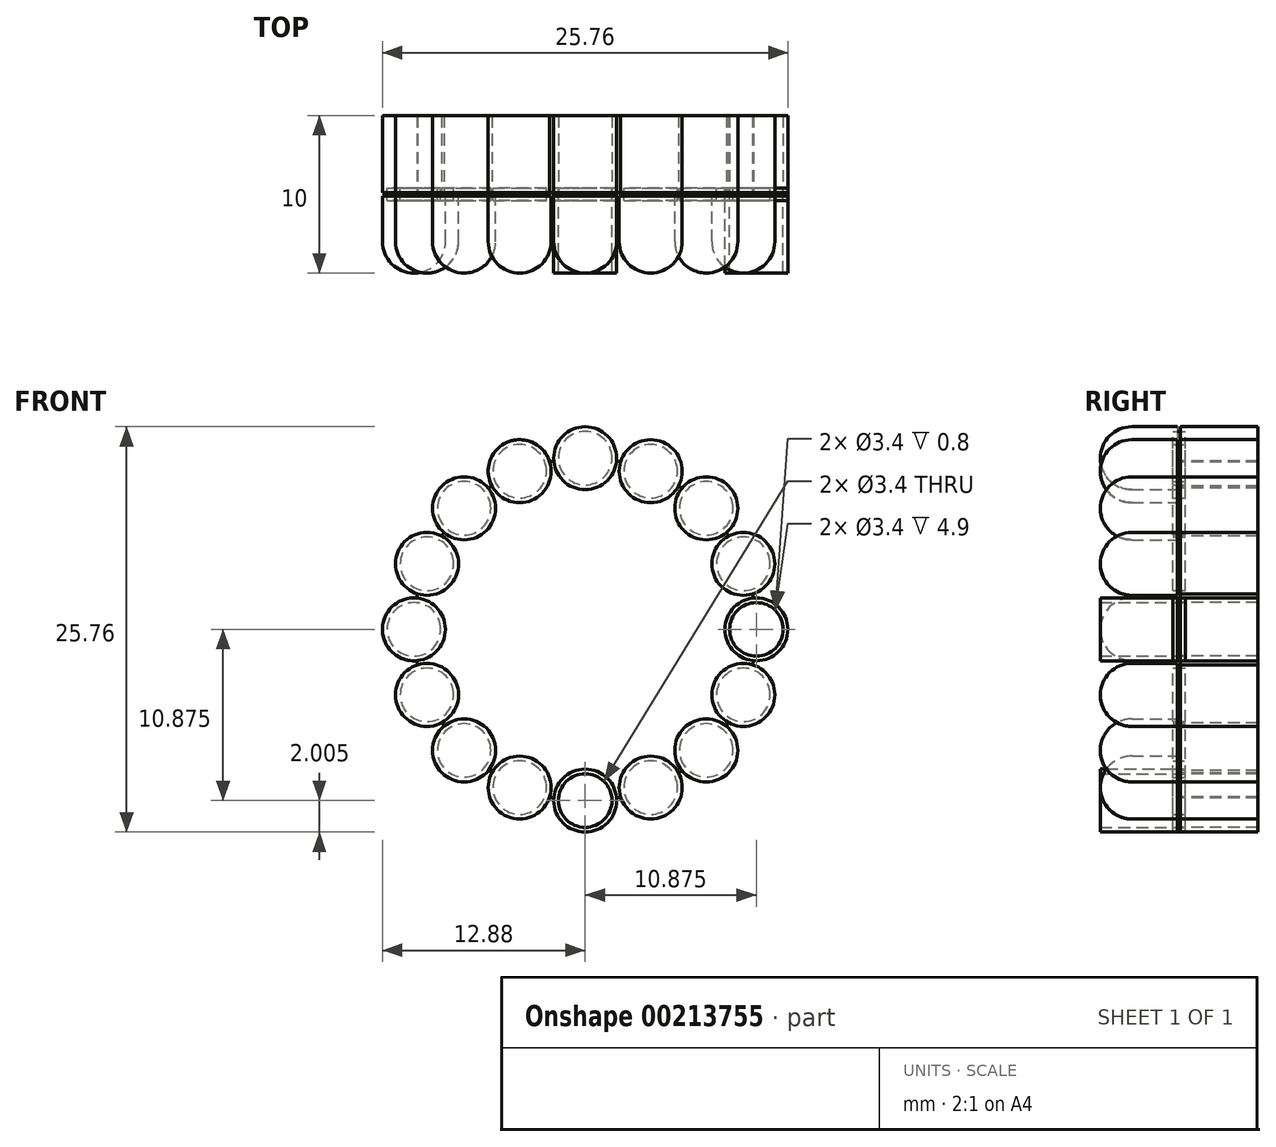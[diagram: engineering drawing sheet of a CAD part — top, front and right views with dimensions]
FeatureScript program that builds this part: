
annotation { "Feature Type Name" : "Feature", "Feature Type Description" : "" }
export const myFeature = defineFeature(function(context is Context, id is Id, definition is map)
    precondition{}
    {
        {
            var Q0;
            Q0=qCreatedBy(makeId("Front.planeOp"),FACE);
            var sketch = newSketch(context, id + "F0", { "sketchPlane" : qUnion([Q0])});
            skCircle(sketch, "E0", {"center": v(0, 0) * mm, "radius": 8.88 * mm, "construction": true});
            skCircle(sketch, "E1.0", {"center": v(0, 0) * mm, "radius": 12.88 * mm, "construction": true});
            skCircle(sketch, "E2.0", {"center": v(0, 0) * mm, "radius": 10.88 * mm});
            skCircle(sketch, "E3", {"center": v(0, 10.88) * mm, "radius": 2 * mm});
            skCircle(sketch, "E4.1.0", {"center": v(-4.16, 10.05) * mm, "radius": 2 * mm});
            skCircle(sketch, "E4.2.0", {"center": v(-7.69, 7.69) * mm, "radius": 2 * mm});
            skCircle(sketch, "E4.3.0", {"center": v(-10.05, 4.16) * mm, "radius": 2 * mm});
            skCircle(sketch, "E4.4.0", {"center": v(-10.88, 0) * mm, "radius": 2 * mm});
            skCircle(sketch, "E4.5.0", {"center": v(-10.05, -4.16) * mm, "radius": 2 * mm});
            skCircle(sketch, "E4.6.0", {"center": v(-7.69, -7.69) * mm, "radius": 2 * mm});
            skCircle(sketch, "E4.7.0", {"center": v(-4.16, -10.05) * mm, "radius": 2 * mm});
            skCircle(sketch, "E4.8.0", {"center": v(0, -10.88) * mm, "radius": 2 * mm});
            skCircle(sketch, "E4.9.0", {"center": v(4.16, -10.05) * mm, "radius": 2 * mm});
            skCircle(sketch, "E4.10.0", {"center": v(7.69, -7.69) * mm, "radius": 2 * mm});
            skCircle(sketch, "E4.11.0", {"center": v(10.05, -4.16) * mm, "radius": 2 * mm});
            skCircle(sketch, "E4.12.0", {"center": v(10.88, 0) * mm, "radius": 2 * mm});
            skCircle(sketch, "E4.13.0", {"center": v(10.05, 4.16) * mm, "radius": 2 * mm});
            skCircle(sketch, "E4.14.0", {"center": v(7.69, 7.69) * mm, "radius": 2 * mm});
            skCircle(sketch, "E4.15.0", {"center": v(4.16, 10.05) * mm, "radius": 2 * mm});
            skCircle(sketch, "E5.0", {"center": v(0, -10.88) * mm, "radius": 1.7 * mm});
            skCircle(sketch, "E6.1.0", {"center": v(4.16, -10.05) * mm, "radius": 1.7 * mm});
            skCircle(sketch, "E6.2.0", {"center": v(7.69, -7.69) * mm, "radius": 1.7 * mm});
            skCircle(sketch, "E6.3.0", {"center": v(10.05, -4.16) * mm, "radius": 1.7 * mm});
            skCircle(sketch, "E6.4.0", {"center": v(10.88, 0) * mm, "radius": 1.7 * mm});
            skCircle(sketch, "E6.5.0", {"center": v(10.05, 4.16) * mm, "radius": 1.7 * mm});
            skCircle(sketch, "E6.6.0", {"center": v(7.69, 7.69) * mm, "radius": 1.7 * mm});
            skCircle(sketch, "E6.7.0", {"center": v(4.16, 10.05) * mm, "radius": 1.7 * mm});
            skCircle(sketch, "E6.8.0", {"center": v(0, 10.88) * mm, "radius": 1.7 * mm});
            skCircle(sketch, "E6.9.0", {"center": v(-4.16, 10.05) * mm, "radius": 1.7 * mm});
            skCircle(sketch, "E6.10.0", {"center": v(-7.69, 7.69) * mm, "radius": 1.7 * mm});
            skCircle(sketch, "E6.11.0", {"center": v(-10.05, 4.16) * mm, "radius": 1.7 * mm});
            skCircle(sketch, "E6.12.0", {"center": v(-10.88, 0) * mm, "radius": 1.7 * mm});
            skCircle(sketch, "E6.13.0", {"center": v(-10.05, -4.16) * mm, "radius": 1.7 * mm});
            skCircle(sketch, "E6.14.0", {"center": v(-7.69, -7.69) * mm, "radius": 1.7 * mm});
            skCircle(sketch, "E6.15.0", {"center": v(-4.16, -10.05) * mm, "radius": 1.7 * mm});
            skSolve(sketch);
        }
        {
            var Q0;
            Q0=makeQuery(id+"F0.imprint","IMPRINT",FACE,{"disambiguationData":[TD([[makeQuery(id+"F0.imprint","IMPRINT",EDGE,{"derivedFrom":sQuery(id+"F0.wireOp",EDGE,"E3")}),1.0]])]});
            var Q1;
            Q1=makeQuery(id+"F0.imprint","IMPRINT",FACE,{"disambiguationData":[TD([[makeQuery(id+"F0.imprint","IMPRINT",EDGE,{"derivedFrom":sQuery(id+"F0.wireOp",EDGE,"E4.15.0")}),1.0]])]});
            var Q2;
            Q2=makeQuery(id+"F0.imprint","IMPRINT",FACE,{"disambiguationData":[TD([[makeQuery(id+"F0.imprint","IMPRINT",EDGE,{"derivedFrom":sQuery(id+"F0.wireOp",EDGE,"E4.14.0")}),1.0]])]});
            var Q3;
            Q3=makeQuery(id+"F0.imprint","IMPRINT",FACE,{"disambiguationData":[TD([[makeQuery(id+"F0.imprint","IMPRINT",EDGE,{"derivedFrom":sQuery(id+"F0.wireOp",EDGE,"E4.13.0")}),1.0]])]});
            var Q4;
            Q4=makeQuery(id+"F0.imprint","IMPRINT",FACE,{"disambiguationData":[TD([[makeQuery(id+"F0.imprint","IMPRINT",EDGE,{"derivedFrom":sQuery(id+"F0.wireOp",EDGE,"E4.12.0")}),1.0]])]});
            var Q5;
            Q5=makeQuery(id+"F0.imprint","IMPRINT",FACE,{"disambiguationData":[TD([[makeQuery(id+"F0.imprint","IMPRINT",EDGE,{"derivedFrom":sQuery(id+"F0.wireOp",EDGE,"E4.11.0")}),1.0]])]});
            var Q6;
            Q6=makeQuery(id+"F0.imprint","IMPRINT",FACE,{"disambiguationData":[TD([[makeQuery(id+"F0.imprint","IMPRINT",EDGE,{"derivedFrom":sQuery(id+"F0.wireOp",EDGE,"E4.10.0")}),1.0]])]});
            var Q7;
            Q7=makeQuery(id+"F0.imprint","IMPRINT",FACE,{"disambiguationData":[TD([[makeQuery(id+"F0.imprint","IMPRINT",EDGE,{"derivedFrom":sQuery(id+"F0.wireOp",EDGE,"E4.9.0")}),1.0]])]});
            var Q8;
            Q8=makeQuery(id+"F0.imprint","IMPRINT",FACE,{"disambiguationData":[TD([[makeQuery(id+"F0.imprint","IMPRINT",EDGE,{"derivedFrom":sQuery(id+"F0.wireOp",EDGE,"E4.8.0")}),1.0]])]});
            var Q9;
            Q9=makeQuery(id+"F0.imprint","IMPRINT",FACE,{"disambiguationData":[TD([[makeQuery(id+"F0.imprint","IMPRINT",EDGE,{"derivedFrom":sQuery(id+"F0.wireOp",EDGE,"E4.7.0")}),1.0]])]});
            var Q10;
            Q10=makeQuery(id+"F0.imprint","IMPRINT",FACE,{"disambiguationData":[TD([[makeQuery(id+"F0.imprint","IMPRINT",EDGE,{"derivedFrom":sQuery(id+"F0.wireOp",EDGE,"E4.6.0")}),1.0]])]});
            var Q11;
            Q11=makeQuery(id+"F0.imprint","IMPRINT",FACE,{"disambiguationData":[TD([[makeQuery(id+"F0.imprint","IMPRINT",EDGE,{"derivedFrom":sQuery(id+"F0.wireOp",EDGE,"E4.5.0")}),1.0]])]});
            var Q12;
            Q12=makeQuery(id+"F0.imprint","IMPRINT",FACE,{"disambiguationData":[TD([[makeQuery(id+"F0.imprint","IMPRINT",EDGE,{"derivedFrom":sQuery(id+"F0.wireOp",EDGE,"E4.4.0")}),1.0]])]});
            var Q13;
            Q13=makeQuery(id+"F0.imprint","IMPRINT",FACE,{"disambiguationData":[TD([[makeQuery(id+"F0.imprint","IMPRINT",EDGE,{"derivedFrom":sQuery(id+"F0.wireOp",EDGE,"E4.3.0")}),1.0]])]});
            var Q14;
            Q14=makeQuery(id+"F0.imprint","IMPRINT",FACE,{"disambiguationData":[TD([[makeQuery(id+"F0.imprint","IMPRINT",EDGE,{"derivedFrom":sQuery(id+"F0.wireOp",EDGE,"E4.2.0")}),1.0]])]});
            var Q15;
            Q15=makeQuery(id+"F0.imprint","IMPRINT",FACE,{"disambiguationData":[TD([[makeQuery(id+"F0.imprint","IMPRINT",EDGE,{"derivedFrom":sQuery(id+"F0.wireOp",EDGE,"E4.1.0")}),1.0]])]});
            var Q16;
            {var subQ0=sQuery(id+"F0.wireOp",EDGE,"E6.3.0");var subQ1=sQuery(id+"F0.wireOp",EDGE,"E2.0");var subQ2=makeQuery(id+"F0.imprint","INTERSECT",VERTEX,{"disambiguationData":[OD(0.0)],"derivedFrom":[subQ1,subQ0]});Q16=makeQuery(id+"F0.imprint","IMPRINT",FACE,{"disambiguationData":[TD([[makeQuery(id+"F0.imprint","IMPRINT",EDGE,{"disambiguationData":[TD([[subQ2,-1.0]])],"derivedFrom":subQ1}),-1.0]])]});}
            var Q17;
            {var subQ0=sQuery(id+"F0.wireOp",EDGE,"E6.3.0");var subQ1=sQuery(id+"F0.wireOp",EDGE,"E2.0");var subQ2=makeQuery(id+"F0.imprint","INTERSECT",VERTEX,{"disambiguationData":[OD(0.0)],"derivedFrom":[subQ1,subQ0]});Q17=makeQuery(id+"F0.imprint","IMPRINT",FACE,{"disambiguationData":[TD([[makeQuery(id+"F0.imprint","IMPRINT",EDGE,{"disambiguationData":[TD([[subQ2,-1.0]])],"derivedFrom":subQ1}),1.0]])]});}
            var Q18;
            {var subQ0=sQuery(id+"F0.wireOp",EDGE,"E6.2.0");var subQ1=sQuery(id+"F0.wireOp",EDGE,"E2.0");var subQ2=makeQuery(id+"F0.imprint","INTERSECT",VERTEX,{"disambiguationData":[OD(0.0)],"derivedFrom":[subQ1,subQ0]});Q18=makeQuery(id+"F0.imprint","IMPRINT",FACE,{"disambiguationData":[TD([[makeQuery(id+"F0.imprint","IMPRINT",EDGE,{"disambiguationData":[TD([[subQ2,-1.0]])],"derivedFrom":subQ1}),-1.0]])]});}
            var Q19;
            {var subQ0=sQuery(id+"F0.wireOp",EDGE,"E6.2.0");var subQ1=sQuery(id+"F0.wireOp",EDGE,"E2.0");var subQ2=makeQuery(id+"F0.imprint","INTERSECT",VERTEX,{"disambiguationData":[OD(0.0)],"derivedFrom":[subQ1,subQ0]});Q19=makeQuery(id+"F0.imprint","IMPRINT",FACE,{"disambiguationData":[TD([[makeQuery(id+"F0.imprint","IMPRINT",EDGE,{"disambiguationData":[TD([[subQ2,-1.0]])],"derivedFrom":subQ1}),1.0]])]});}
            var Q20;
            {var subQ0=sQuery(id+"F0.wireOp",EDGE,"E6.1.0");var subQ1=sQuery(id+"F0.wireOp",EDGE,"E2.0");var subQ2=makeQuery(id+"F0.imprint","INTERSECT",VERTEX,{"disambiguationData":[OD(0.0)],"derivedFrom":[subQ1,subQ0]});Q20=makeQuery(id+"F0.imprint","IMPRINT",FACE,{"disambiguationData":[TD([[makeQuery(id+"F0.imprint","IMPRINT",EDGE,{"disambiguationData":[TD([[subQ2,-1.0]])],"derivedFrom":subQ1}),-1.0]])]});}
            var Q21;
            {var subQ0=sQuery(id+"F0.wireOp",EDGE,"E6.1.0");var subQ1=sQuery(id+"F0.wireOp",EDGE,"E2.0");var subQ2=makeQuery(id+"F0.imprint","INTERSECT",VERTEX,{"disambiguationData":[OD(0.0)],"derivedFrom":[subQ1,subQ0]});Q21=makeQuery(id+"F0.imprint","IMPRINT",FACE,{"disambiguationData":[TD([[makeQuery(id+"F0.imprint","IMPRINT",EDGE,{"disambiguationData":[TD([[subQ2,-1.0]])],"derivedFrom":subQ1}),1.0]])]});}
            var Q22;
            {var subQ0=sQuery(id+"F0.wireOp",EDGE,"E5.0");var subQ1=sQuery(id+"F0.wireOp",EDGE,"E2.0");var subQ2=makeQuery(id+"F0.imprint","INTERSECT",VERTEX,{"disambiguationData":[OD(0.0)],"derivedFrom":[subQ1,subQ0]});Q22=makeQuery(id+"F0.imprint","IMPRINT",FACE,{"disambiguationData":[TD([[makeQuery(id+"F0.imprint","IMPRINT",EDGE,{"disambiguationData":[TD([[subQ2,-1.0]])],"derivedFrom":subQ1}),-1.0]])]});}
            var Q23;
            {var subQ0=sQuery(id+"F0.wireOp",EDGE,"E5.0");var subQ1=sQuery(id+"F0.wireOp",EDGE,"E2.0");var subQ2=makeQuery(id+"F0.imprint","INTERSECT",VERTEX,{"disambiguationData":[OD(0.0)],"derivedFrom":[subQ1,subQ0]});Q23=makeQuery(id+"F0.imprint","IMPRINT",FACE,{"disambiguationData":[TD([[makeQuery(id+"F0.imprint","IMPRINT",EDGE,{"disambiguationData":[TD([[subQ2,-1.0]])],"derivedFrom":subQ1}),1.0]])]});}
            var Q24;
            {var subQ0=sQuery(id+"F0.wireOp",EDGE,"E6.15.0");var subQ1=sQuery(id+"F0.wireOp",EDGE,"E2.0");var subQ2=makeQuery(id+"F0.imprint","INTERSECT",VERTEX,{"disambiguationData":[OD(0.0)],"derivedFrom":[subQ1,subQ0]});Q24=makeQuery(id+"F0.imprint","IMPRINT",FACE,{"disambiguationData":[TD([[makeQuery(id+"F0.imprint","IMPRINT",EDGE,{"disambiguationData":[TD([[subQ2,-1.0]])],"derivedFrom":subQ1}),-1.0]])]});}
            var Q25;
            {var subQ0=sQuery(id+"F0.wireOp",EDGE,"E6.15.0");var subQ1=sQuery(id+"F0.wireOp",EDGE,"E2.0");var subQ2=makeQuery(id+"F0.imprint","INTERSECT",VERTEX,{"disambiguationData":[OD(0.0)],"derivedFrom":[subQ1,subQ0]});Q25=makeQuery(id+"F0.imprint","IMPRINT",FACE,{"disambiguationData":[TD([[makeQuery(id+"F0.imprint","IMPRINT",EDGE,{"disambiguationData":[TD([[subQ2,-1.0]])],"derivedFrom":subQ1}),1.0]])]});}
            var Q26;
            {var subQ0=sQuery(id+"F0.wireOp",EDGE,"E6.14.0");var subQ1=sQuery(id+"F0.wireOp",EDGE,"E2.0");var subQ2=makeQuery(id+"F0.imprint","INTERSECT",VERTEX,{"disambiguationData":[OD(0.0)],"derivedFrom":[subQ1,subQ0]});Q26=makeQuery(id+"F0.imprint","IMPRINT",FACE,{"disambiguationData":[TD([[makeQuery(id+"F0.imprint","IMPRINT",EDGE,{"disambiguationData":[TD([[subQ2,-1.0]])],"derivedFrom":subQ1}),-1.0]])]});}
            var Q27;
            {var subQ0=sQuery(id+"F0.wireOp",EDGE,"E6.14.0");var subQ1=sQuery(id+"F0.wireOp",EDGE,"E2.0");var subQ2=makeQuery(id+"F0.imprint","INTERSECT",VERTEX,{"disambiguationData":[OD(0.0)],"derivedFrom":[subQ1,subQ0]});Q27=makeQuery(id+"F0.imprint","IMPRINT",FACE,{"disambiguationData":[TD([[makeQuery(id+"F0.imprint","IMPRINT",EDGE,{"disambiguationData":[TD([[subQ2,-1.0]])],"derivedFrom":subQ1}),1.0]])]});}
            var Q28;
            {var subQ0=sQuery(id+"F0.wireOp",EDGE,"E6.13.0");var subQ1=sQuery(id+"F0.wireOp",EDGE,"E2.0");var subQ2=makeQuery(id+"F0.imprint","INTERSECT",VERTEX,{"disambiguationData":[OD(0.0)],"derivedFrom":[subQ1,subQ0]});Q28=makeQuery(id+"F0.imprint","IMPRINT",FACE,{"disambiguationData":[TD([[makeQuery(id+"F0.imprint","IMPRINT",EDGE,{"disambiguationData":[TD([[subQ2,-1.0]])],"derivedFrom":subQ1}),-1.0]])]});}
            var Q29;
            {var subQ0=sQuery(id+"F0.wireOp",EDGE,"E6.13.0");var subQ1=sQuery(id+"F0.wireOp",EDGE,"E2.0");var subQ2=makeQuery(id+"F0.imprint","INTERSECT",VERTEX,{"disambiguationData":[OD(0.0)],"derivedFrom":[subQ1,subQ0]});Q29=makeQuery(id+"F0.imprint","IMPRINT",FACE,{"disambiguationData":[TD([[makeQuery(id+"F0.imprint","IMPRINT",EDGE,{"disambiguationData":[TD([[subQ2,-1.0]])],"derivedFrom":subQ1}),1.0]])]});}
            var Q30;
            {var subQ0=sQuery(id+"F0.wireOp",EDGE,"E6.12.0");var subQ1=sQuery(id+"F0.wireOp",EDGE,"E2.0");var subQ2=makeQuery(id+"F0.imprint","INTERSECT",VERTEX,{"disambiguationData":[OD(0.0)],"derivedFrom":[subQ1,subQ0]});Q30=makeQuery(id+"F0.imprint","IMPRINT",FACE,{"disambiguationData":[TD([[makeQuery(id+"F0.imprint","IMPRINT",EDGE,{"disambiguationData":[TD([[subQ2,-1.0]])],"derivedFrom":subQ1}),-1.0]])]});}
            var Q31;
            {var subQ0=sQuery(id+"F0.wireOp",EDGE,"E6.12.0");var subQ1=sQuery(id+"F0.wireOp",EDGE,"E2.0");var subQ2=makeQuery(id+"F0.imprint","INTERSECT",VERTEX,{"disambiguationData":[OD(0.0)],"derivedFrom":[subQ1,subQ0]});Q31=makeQuery(id+"F0.imprint","IMPRINT",FACE,{"disambiguationData":[TD([[makeQuery(id+"F0.imprint","IMPRINT",EDGE,{"disambiguationData":[TD([[subQ2,-1.0]])],"derivedFrom":subQ1}),1.0]])]});}
            var Q32;
            {var subQ0=sQuery(id+"F0.wireOp",EDGE,"E6.11.0");var subQ1=sQuery(id+"F0.wireOp",EDGE,"E2.0");var subQ2=makeQuery(id+"F0.imprint","INTERSECT",VERTEX,{"disambiguationData":[OD(0.0)],"derivedFrom":[subQ1,subQ0]});Q32=makeQuery(id+"F0.imprint","IMPRINT",FACE,{"disambiguationData":[TD([[makeQuery(id+"F0.imprint","IMPRINT",EDGE,{"disambiguationData":[TD([[subQ2,-1.0]])],"derivedFrom":subQ1}),-1.0]])]});}
            var Q33;
            {var subQ0=sQuery(id+"F0.wireOp",EDGE,"E6.11.0");var subQ1=sQuery(id+"F0.wireOp",EDGE,"E2.0");var subQ2=makeQuery(id+"F0.imprint","INTERSECT",VERTEX,{"disambiguationData":[OD(0.0)],"derivedFrom":[subQ1,subQ0]});Q33=makeQuery(id+"F0.imprint","IMPRINT",FACE,{"disambiguationData":[TD([[makeQuery(id+"F0.imprint","IMPRINT",EDGE,{"disambiguationData":[TD([[subQ2,-1.0]])],"derivedFrom":subQ1}),1.0]])]});}
            var Q34;
            {var subQ0=sQuery(id+"F0.wireOp",EDGE,"E6.10.0");var subQ1=sQuery(id+"F0.wireOp",EDGE,"E2.0");var subQ2=makeQuery(id+"F0.imprint","INTERSECT",VERTEX,{"disambiguationData":[OD(0.0)],"derivedFrom":[subQ1,subQ0]});Q34=makeQuery(id+"F0.imprint","IMPRINT",FACE,{"disambiguationData":[TD([[makeQuery(id+"F0.imprint","IMPRINT",EDGE,{"disambiguationData":[TD([[subQ2,-1.0]])],"derivedFrom":subQ1}),-1.0]])]});}
            var Q35;
            {var subQ0=sQuery(id+"F0.wireOp",EDGE,"E6.10.0");var subQ1=sQuery(id+"F0.wireOp",EDGE,"E2.0");var subQ2=makeQuery(id+"F0.imprint","INTERSECT",VERTEX,{"disambiguationData":[OD(0.0)],"derivedFrom":[subQ1,subQ0]});Q35=makeQuery(id+"F0.imprint","IMPRINT",FACE,{"disambiguationData":[TD([[makeQuery(id+"F0.imprint","IMPRINT",EDGE,{"disambiguationData":[TD([[subQ2,-1.0]])],"derivedFrom":subQ1}),1.0]])]});}
            var Q36;
            {var subQ0=sQuery(id+"F0.wireOp",EDGE,"E6.9.0");var subQ1=sQuery(id+"F0.wireOp",EDGE,"E2.0");var subQ2=makeQuery(id+"F0.imprint","INTERSECT",VERTEX,{"disambiguationData":[OD(0.0)],"derivedFrom":[subQ1,subQ0]});Q36=makeQuery(id+"F0.imprint","IMPRINT",FACE,{"disambiguationData":[TD([[makeQuery(id+"F0.imprint","IMPRINT",EDGE,{"disambiguationData":[TD([[subQ2,-1.0]])],"derivedFrom":subQ1}),-1.0]])]});}
            var Q37;
            {var subQ0=sQuery(id+"F0.wireOp",EDGE,"E6.9.0");var subQ1=sQuery(id+"F0.wireOp",EDGE,"E2.0");var subQ2=makeQuery(id+"F0.imprint","INTERSECT",VERTEX,{"disambiguationData":[OD(0.0)],"derivedFrom":[subQ1,subQ0]});Q37=makeQuery(id+"F0.imprint","IMPRINT",FACE,{"disambiguationData":[TD([[makeQuery(id+"F0.imprint","IMPRINT",EDGE,{"disambiguationData":[TD([[subQ2,-1.0]])],"derivedFrom":subQ1}),1.0]])]});}
            var Q38;
            {var subQ0=sQuery(id+"F0.wireOp",EDGE,"E6.8.0");var subQ1=sQuery(id+"F0.wireOp",EDGE,"E2.0");var subQ2=makeQuery(id+"F0.imprint","INTERSECT",VERTEX,{"disambiguationData":[OD(0.0)],"derivedFrom":[subQ1,subQ0]});Q38=makeQuery(id+"F0.imprint","IMPRINT",FACE,{"disambiguationData":[TD([[makeQuery(id+"F0.imprint","IMPRINT",EDGE,{"disambiguationData":[TD([[subQ2,-1.0]])],"derivedFrom":subQ1}),-1.0]])]});}
            var Q39;
            {var subQ0=sQuery(id+"F0.wireOp",EDGE,"E6.8.0");var subQ1=sQuery(id+"F0.wireOp",EDGE,"E2.0");var subQ2=makeQuery(id+"F0.imprint","INTERSECT",VERTEX,{"disambiguationData":[OD(0.0)],"derivedFrom":[subQ1,subQ0]});Q39=makeQuery(id+"F0.imprint","IMPRINT",FACE,{"disambiguationData":[TD([[makeQuery(id+"F0.imprint","IMPRINT",EDGE,{"disambiguationData":[TD([[subQ2,-1.0]])],"derivedFrom":subQ1}),1.0]])]});}
            var Q40;
            {var subQ0=sQuery(id+"F0.wireOp",EDGE,"E6.7.0");var subQ1=sQuery(id+"F0.wireOp",EDGE,"E2.0");var subQ2=makeQuery(id+"F0.imprint","INTERSECT",VERTEX,{"disambiguationData":[OD(0.0)],"derivedFrom":[subQ1,subQ0]});Q40=makeQuery(id+"F0.imprint","IMPRINT",FACE,{"disambiguationData":[TD([[makeQuery(id+"F0.imprint","IMPRINT",EDGE,{"disambiguationData":[TD([[subQ2,-1.0]])],"derivedFrom":subQ1}),-1.0]])]});}
            var Q41;
            {var subQ0=sQuery(id+"F0.wireOp",EDGE,"E6.7.0");var subQ1=sQuery(id+"F0.wireOp",EDGE,"E2.0");var subQ2=makeQuery(id+"F0.imprint","INTERSECT",VERTEX,{"disambiguationData":[OD(0.0)],"derivedFrom":[subQ1,subQ0]});Q41=makeQuery(id+"F0.imprint","IMPRINT",FACE,{"disambiguationData":[TD([[makeQuery(id+"F0.imprint","IMPRINT",EDGE,{"disambiguationData":[TD([[subQ2,-1.0]])],"derivedFrom":subQ1}),1.0]])]});}
            var Q42;
            {var subQ0=sQuery(id+"F0.wireOp",EDGE,"E6.6.0");var subQ1=sQuery(id+"F0.wireOp",EDGE,"E2.0");var subQ2=makeQuery(id+"F0.imprint","INTERSECT",VERTEX,{"disambiguationData":[OD(0.0)],"derivedFrom":[subQ1,subQ0]});Q42=makeQuery(id+"F0.imprint","IMPRINT",FACE,{"disambiguationData":[TD([[makeQuery(id+"F0.imprint","IMPRINT",EDGE,{"disambiguationData":[TD([[subQ2,-1.0]])],"derivedFrom":subQ1}),-1.0]])]});}
            var Q43;
            {var subQ0=sQuery(id+"F0.wireOp",EDGE,"E6.6.0");var subQ1=sQuery(id+"F0.wireOp",EDGE,"E2.0");var subQ2=makeQuery(id+"F0.imprint","INTERSECT",VERTEX,{"disambiguationData":[OD(0.0)],"derivedFrom":[subQ1,subQ0]});Q43=makeQuery(id+"F0.imprint","IMPRINT",FACE,{"disambiguationData":[TD([[makeQuery(id+"F0.imprint","IMPRINT",EDGE,{"disambiguationData":[TD([[subQ2,-1.0]])],"derivedFrom":subQ1}),1.0]])]});}
            var Q44;
            {var subQ0=sQuery(id+"F0.wireOp",EDGE,"E6.5.0");var subQ1=sQuery(id+"F0.wireOp",EDGE,"E2.0");var subQ2=makeQuery(id+"F0.imprint","INTERSECT",VERTEX,{"disambiguationData":[OD(0.0)],"derivedFrom":[subQ1,subQ0]});Q44=makeQuery(id+"F0.imprint","IMPRINT",FACE,{"disambiguationData":[TD([[makeQuery(id+"F0.imprint","IMPRINT",EDGE,{"disambiguationData":[TD([[subQ2,-1.0]])],"derivedFrom":subQ1}),-1.0]])]});}
            var Q45;
            {var subQ0=sQuery(id+"F0.wireOp",EDGE,"E6.5.0");var subQ1=sQuery(id+"F0.wireOp",EDGE,"E2.0");var subQ2=makeQuery(id+"F0.imprint","INTERSECT",VERTEX,{"disambiguationData":[OD(0.0)],"derivedFrom":[subQ1,subQ0]});Q45=makeQuery(id+"F0.imprint","IMPRINT",FACE,{"disambiguationData":[TD([[makeQuery(id+"F0.imprint","IMPRINT",EDGE,{"disambiguationData":[TD([[subQ2,-1.0]])],"derivedFrom":subQ1}),1.0]])]});}
            var Q46;
            {var subQ0=sQuery(id+"F0.wireOp",EDGE,"E6.4.0");var subQ1=sQuery(id+"F0.wireOp",EDGE,"E2.0");var subQ2=makeQuery(id+"F0.imprint","INTERSECT",VERTEX,{"disambiguationData":[OD(0.0)],"derivedFrom":[subQ1,subQ0]});Q46=makeQuery(id+"F0.imprint","IMPRINT",FACE,{"disambiguationData":[TD([[makeQuery(id+"F0.imprint","IMPRINT",EDGE,{"disambiguationData":[TD([[subQ2,1.0]])],"derivedFrom":subQ1}),-1.0]])]});}
            var Q47;
            {var subQ0=sQuery(id+"F0.wireOp",EDGE,"E6.4.0");var subQ1=sQuery(id+"F0.wireOp",EDGE,"E2.0");var subQ2=makeQuery(id+"F0.imprint","INTERSECT",VERTEX,{"disambiguationData":[OD(0.0)],"derivedFrom":[subQ1,subQ0]});Q47=makeQuery(id+"F0.imprint","IMPRINT",FACE,{"disambiguationData":[TD([[makeQuery(id+"F0.imprint","IMPRINT",EDGE,{"disambiguationData":[TD([[subQ2,1.0]])],"derivedFrom":subQ1}),1.0]])]});}
            extrude(context, id + "F1", {"entities" : qUnion([Q0, Q1, Q2, Q3, Q4, Q5, Q6, Q7, Q8, Q9, Q10, Q11, Q12, Q13, Q14, Q15, Q16, Q17, Q18, Q19, Q20, Q21, Q22, Q23, Q24, Q25, Q26, Q27, Q28, Q29, Q30, Q31, Q32, Q33, Q34, Q35, Q36, Q37, Q38, Q39, Q40, Q41, Q42, Q43, Q44, Q45, Q46, Q47]), "depth" : 5 * mm, "hasSecondDirection" : true, "secondDirectionOppositeDirection" : false, "secondDirectionDepth" : .1 * mm});
        }
        {
            var Q0;
            Q0=qCreatedBy(makeId("Right.planeOp"),FACE);
            var sketch = newSketch(context, id + "F2", { "sketchPlane" : qUnion([Q0])});
            skPoint(sketch, "E7", {"position": v(0, -10.88) * mm});
            skCircle(sketch, "E8", {"center": v(0, -10.88) * mm, "radius": 0.5 * mm});
            skSolve(sketch);
        }
        {
            var Q0;
            Q0=sQuery(id+"F2.wireOp",EDGE,"E8");
            var Q1;
            Q1=sQuery(id+"F0.wireOp",EDGE,"E2.0");
            revolve(context, id + "F3", {"bodyType" : ToolBodyType.SURFACE, "surfaceEntities" : qUnion([Q0]), "axis" : qUnion([Q1]), "revolveType" : RevolveType.FULL});
        }
        {
            var Q0;
            {var subQ0=sQuery(id+"F0.wireOp",EDGE,"E6.3.0");var subQ1=sQuery(id+"F0.wireOp",EDGE,"E2.0");var subQ2=makeQuery(id+"F0.imprint","INTERSECT",VERTEX,{"disambiguationData":[OD(0.0)],"derivedFrom":[subQ1,subQ0]});Q0=makeQuery(id+"F0.imprint","IMPRINT",FACE,{"disambiguationData":[TD([[makeQuery(id+"F0.imprint","IMPRINT",EDGE,{"disambiguationData":[TD([[subQ2,-1.0]])],"derivedFrom":subQ1}),-1.0]])]});}
            var Q1;
            {var subQ0=sQuery(id+"F0.wireOp",EDGE,"E4.11.0");var subQ1=sQuery(id+"F0.wireOp",EDGE,"E2.0");var subQ2=makeQuery(id+"F0.imprint","INTERSECT",VERTEX,{"disambiguationData":[OD(0.0)],"derivedFrom":[subQ1,subQ0]});Q1=makeQuery(id+"F0.imprint","IMPRINT",FACE,{"disambiguationData":[TD([[makeQuery(id+"F0.imprint","IMPRINT",EDGE,{"disambiguationData":[TD([[subQ2,-1.0]])],"derivedFrom":subQ1}),-1.0]])]});}
            var Q2;
            {var subQ0=sQuery(id+"F0.wireOp",EDGE,"E6.3.0");var subQ1=sQuery(id+"F0.wireOp",EDGE,"E2.0");var subQ2=makeQuery(id+"F0.imprint","INTERSECT",VERTEX,{"disambiguationData":[OD(0.0)],"derivedFrom":[subQ1,subQ0]});Q2=makeQuery(id+"F0.imprint","IMPRINT",FACE,{"disambiguationData":[TD([[makeQuery(id+"F0.imprint","IMPRINT",EDGE,{"disambiguationData":[TD([[subQ2,-1.0]])],"derivedFrom":subQ1}),1.0]])]});}
            var Q3;
            {var subQ0=sQuery(id+"F0.wireOp",EDGE,"E4.11.0");var subQ1=sQuery(id+"F0.wireOp",EDGE,"E2.0");var subQ2=makeQuery(id+"F0.imprint","INTERSECT",VERTEX,{"disambiguationData":[OD(0.0)],"derivedFrom":[subQ1,subQ0]});Q3=makeQuery(id+"F0.imprint","IMPRINT",FACE,{"disambiguationData":[TD([[makeQuery(id+"F0.imprint","IMPRINT",EDGE,{"disambiguationData":[TD([[subQ2,-1.0]])],"derivedFrom":subQ1}),1.0]])]});}
            var Q4;
            {var subQ0=sQuery(id+"F0.wireOp",EDGE,"E4.10.0");var subQ1=sQuery(id+"F0.wireOp",EDGE,"E2.0");var subQ2=makeQuery(id+"F0.imprint","INTERSECT",VERTEX,{"disambiguationData":[OD(0.0)],"derivedFrom":[subQ1,subQ0]});Q4=makeQuery(id+"F0.imprint","IMPRINT",FACE,{"disambiguationData":[TD([[makeQuery(id+"F0.imprint","IMPRINT",EDGE,{"disambiguationData":[TD([[subQ2,-1.0]])],"derivedFrom":subQ1}),1.0]])]});}
            var Q5;
            {var subQ0=sQuery(id+"F0.wireOp",EDGE,"E6.2.0");var subQ1=sQuery(id+"F0.wireOp",EDGE,"E2.0");var subQ2=makeQuery(id+"F0.imprint","INTERSECT",VERTEX,{"disambiguationData":[OD(0.0)],"derivedFrom":[subQ1,subQ0]});Q5=makeQuery(id+"F0.imprint","IMPRINT",FACE,{"disambiguationData":[TD([[makeQuery(id+"F0.imprint","IMPRINT",EDGE,{"disambiguationData":[TD([[subQ2,-1.0]])],"derivedFrom":subQ1}),1.0]])]});}
            var Q6;
            {var subQ0=sQuery(id+"F0.wireOp",EDGE,"E6.2.0");var subQ1=sQuery(id+"F0.wireOp",EDGE,"E2.0");var subQ2=makeQuery(id+"F0.imprint","INTERSECT",VERTEX,{"disambiguationData":[OD(0.0)],"derivedFrom":[subQ1,subQ0]});Q6=makeQuery(id+"F0.imprint","IMPRINT",FACE,{"disambiguationData":[TD([[makeQuery(id+"F0.imprint","IMPRINT",EDGE,{"disambiguationData":[TD([[subQ2,-1.0]])],"derivedFrom":subQ1}),-1.0]])]});}
            var Q7;
            {var subQ0=sQuery(id+"F0.wireOp",EDGE,"E4.10.0");var subQ1=sQuery(id+"F0.wireOp",EDGE,"E2.0");var subQ2=makeQuery(id+"F0.imprint","INTERSECT",VERTEX,{"disambiguationData":[OD(0.0)],"derivedFrom":[subQ1,subQ0]});Q7=makeQuery(id+"F0.imprint","IMPRINT",FACE,{"disambiguationData":[TD([[makeQuery(id+"F0.imprint","IMPRINT",EDGE,{"disambiguationData":[TD([[subQ2,-1.0]])],"derivedFrom":subQ1}),-1.0]])]});}
            var Q8;
            {var subQ0=sQuery(id+"F0.wireOp",EDGE,"E4.9.0");var subQ1=sQuery(id+"F0.wireOp",EDGE,"E2.0");var subQ2=makeQuery(id+"F0.imprint","INTERSECT",VERTEX,{"disambiguationData":[OD(0.0)],"derivedFrom":[subQ1,subQ0]});Q8=makeQuery(id+"F0.imprint","IMPRINT",FACE,{"disambiguationData":[TD([[makeQuery(id+"F0.imprint","IMPRINT",EDGE,{"disambiguationData":[TD([[subQ2,-1.0]])],"derivedFrom":subQ1}),-1.0]])]});}
            var Q9;
            {var subQ0=sQuery(id+"F0.wireOp",EDGE,"E6.1.0");var subQ1=sQuery(id+"F0.wireOp",EDGE,"E2.0");var subQ2=makeQuery(id+"F0.imprint","INTERSECT",VERTEX,{"disambiguationData":[OD(0.0)],"derivedFrom":[subQ1,subQ0]});Q9=makeQuery(id+"F0.imprint","IMPRINT",FACE,{"disambiguationData":[TD([[makeQuery(id+"F0.imprint","IMPRINT",EDGE,{"disambiguationData":[TD([[subQ2,-1.0]])],"derivedFrom":subQ1}),-1.0]])]});}
            var Q10;
            {var subQ0=sQuery(id+"F0.wireOp",EDGE,"E6.1.0");var subQ1=sQuery(id+"F0.wireOp",EDGE,"E2.0");var subQ2=makeQuery(id+"F0.imprint","INTERSECT",VERTEX,{"disambiguationData":[OD(0.0)],"derivedFrom":[subQ1,subQ0]});Q10=makeQuery(id+"F0.imprint","IMPRINT",FACE,{"disambiguationData":[TD([[makeQuery(id+"F0.imprint","IMPRINT",EDGE,{"disambiguationData":[TD([[subQ2,-1.0]])],"derivedFrom":subQ1}),1.0]])]});}
            var Q11;
            {var subQ0=sQuery(id+"F0.wireOp",EDGE,"E4.9.0");var subQ1=sQuery(id+"F0.wireOp",EDGE,"E2.0");var subQ2=makeQuery(id+"F0.imprint","INTERSECT",VERTEX,{"disambiguationData":[OD(0.0)],"derivedFrom":[subQ1,subQ0]});Q11=makeQuery(id+"F0.imprint","IMPRINT",FACE,{"disambiguationData":[TD([[makeQuery(id+"F0.imprint","IMPRINT",EDGE,{"disambiguationData":[TD([[subQ2,-1.0]])],"derivedFrom":subQ1}),1.0]])]});}
            var Q12;
            {var subQ0=sQuery(id+"F0.wireOp",EDGE,"E5.0");var subQ1=sQuery(id+"F0.wireOp",EDGE,"E2.0");var subQ2=makeQuery(id+"F0.imprint","INTERSECT",VERTEX,{"disambiguationData":[OD(0.0)],"derivedFrom":[subQ1,subQ0]});Q12=makeQuery(id+"F0.imprint","IMPRINT",FACE,{"disambiguationData":[TD([[makeQuery(id+"F0.imprint","IMPRINT",EDGE,{"disambiguationData":[TD([[subQ2,-1.0]])],"derivedFrom":subQ1}),1.0]])]});}
            var Q13;
            {var subQ0=sQuery(id+"F0.wireOp",EDGE,"E5.0");var subQ1=sQuery(id+"F0.wireOp",EDGE,"E2.0");var subQ2=makeQuery(id+"F0.imprint","INTERSECT",VERTEX,{"disambiguationData":[OD(0.0)],"derivedFrom":[subQ1,subQ0]});Q13=makeQuery(id+"F0.imprint","IMPRINT",FACE,{"disambiguationData":[TD([[makeQuery(id+"F0.imprint","IMPRINT",EDGE,{"disambiguationData":[TD([[subQ2,-1.0]])],"derivedFrom":subQ1}),-1.0]])]});}
            var Q14;
            {var subQ0=sQuery(id+"F0.wireOp",EDGE,"E4.8.0");var subQ1=sQuery(id+"F0.wireOp",EDGE,"E2.0");var subQ2=makeQuery(id+"F0.imprint","INTERSECT",VERTEX,{"disambiguationData":[OD(0.0)],"derivedFrom":[subQ1,subQ0]});Q14=makeQuery(id+"F0.imprint","IMPRINT",FACE,{"disambiguationData":[TD([[makeQuery(id+"F0.imprint","IMPRINT",EDGE,{"disambiguationData":[TD([[subQ2,-1.0]])],"derivedFrom":subQ1}),-1.0]])]});}
            var Q15;
            {var subQ0=sQuery(id+"F0.wireOp",EDGE,"E4.8.0");var subQ1=sQuery(id+"F0.wireOp",EDGE,"E2.0");var subQ2=makeQuery(id+"F0.imprint","INTERSECT",VERTEX,{"disambiguationData":[OD(0.0)],"derivedFrom":[subQ1,subQ0]});Q15=makeQuery(id+"F0.imprint","IMPRINT",FACE,{"disambiguationData":[TD([[makeQuery(id+"F0.imprint","IMPRINT",EDGE,{"disambiguationData":[TD([[subQ2,-1.0]])],"derivedFrom":subQ1}),1.0]])]});}
            var Q16;
            {var subQ0=sQuery(id+"F0.wireOp",EDGE,"E4.7.0");var subQ1=sQuery(id+"F0.wireOp",EDGE,"E2.0");var subQ2=makeQuery(id+"F0.imprint","INTERSECT",VERTEX,{"disambiguationData":[OD(0.0)],"derivedFrom":[subQ1,subQ0]});Q16=makeQuery(id+"F0.imprint","IMPRINT",FACE,{"disambiguationData":[TD([[makeQuery(id+"F0.imprint","IMPRINT",EDGE,{"disambiguationData":[TD([[subQ2,-1.0]])],"derivedFrom":subQ1}),1.0]])]});}
            var Q17;
            {var subQ0=sQuery(id+"F0.wireOp",EDGE,"E6.15.0");var subQ1=sQuery(id+"F0.wireOp",EDGE,"E2.0");var subQ2=makeQuery(id+"F0.imprint","INTERSECT",VERTEX,{"disambiguationData":[OD(0.0)],"derivedFrom":[subQ1,subQ0]});Q17=makeQuery(id+"F0.imprint","IMPRINT",FACE,{"disambiguationData":[TD([[makeQuery(id+"F0.imprint","IMPRINT",EDGE,{"disambiguationData":[TD([[subQ2,-1.0]])],"derivedFrom":subQ1}),1.0]])]});}
            var Q18;
            {var subQ0=sQuery(id+"F0.wireOp",EDGE,"E6.15.0");var subQ1=sQuery(id+"F0.wireOp",EDGE,"E2.0");var subQ2=makeQuery(id+"F0.imprint","INTERSECT",VERTEX,{"disambiguationData":[OD(0.0)],"derivedFrom":[subQ1,subQ0]});Q18=makeQuery(id+"F0.imprint","IMPRINT",FACE,{"disambiguationData":[TD([[makeQuery(id+"F0.imprint","IMPRINT",EDGE,{"disambiguationData":[TD([[subQ2,-1.0]])],"derivedFrom":subQ1}),-1.0]])]});}
            var Q19;
            {var subQ0=sQuery(id+"F0.wireOp",EDGE,"E4.7.0");var subQ1=sQuery(id+"F0.wireOp",EDGE,"E2.0");var subQ2=makeQuery(id+"F0.imprint","INTERSECT",VERTEX,{"disambiguationData":[OD(0.0)],"derivedFrom":[subQ1,subQ0]});Q19=makeQuery(id+"F0.imprint","IMPRINT",FACE,{"disambiguationData":[TD([[makeQuery(id+"F0.imprint","IMPRINT",EDGE,{"disambiguationData":[TD([[subQ2,-1.0]])],"derivedFrom":subQ1}),-1.0]])]});}
            var Q20;
            {var subQ0=sQuery(id+"F0.wireOp",EDGE,"E4.6.0");var subQ1=sQuery(id+"F0.wireOp",EDGE,"E2.0");var subQ2=makeQuery(id+"F0.imprint","INTERSECT",VERTEX,{"disambiguationData":[OD(0.0)],"derivedFrom":[subQ1,subQ0]});Q20=makeQuery(id+"F0.imprint","IMPRINT",FACE,{"disambiguationData":[TD([[makeQuery(id+"F0.imprint","IMPRINT",EDGE,{"disambiguationData":[TD([[subQ2,-1.0]])],"derivedFrom":subQ1}),-1.0]])]});}
            var Q21;
            {var subQ0=sQuery(id+"F0.wireOp",EDGE,"E6.14.0");var subQ1=sQuery(id+"F0.wireOp",EDGE,"E2.0");var subQ2=makeQuery(id+"F0.imprint","INTERSECT",VERTEX,{"disambiguationData":[OD(0.0)],"derivedFrom":[subQ1,subQ0]});Q21=makeQuery(id+"F0.imprint","IMPRINT",FACE,{"disambiguationData":[TD([[makeQuery(id+"F0.imprint","IMPRINT",EDGE,{"disambiguationData":[TD([[subQ2,-1.0]])],"derivedFrom":subQ1}),-1.0]])]});}
            var Q22;
            {var subQ0=sQuery(id+"F0.wireOp",EDGE,"E6.14.0");var subQ1=sQuery(id+"F0.wireOp",EDGE,"E2.0");var subQ2=makeQuery(id+"F0.imprint","INTERSECT",VERTEX,{"disambiguationData":[OD(0.0)],"derivedFrom":[subQ1,subQ0]});Q22=makeQuery(id+"F0.imprint","IMPRINT",FACE,{"disambiguationData":[TD([[makeQuery(id+"F0.imprint","IMPRINT",EDGE,{"disambiguationData":[TD([[subQ2,-1.0]])],"derivedFrom":subQ1}),1.0]])]});}
            var Q23;
            {var subQ0=sQuery(id+"F0.wireOp",EDGE,"E4.6.0");var subQ1=sQuery(id+"F0.wireOp",EDGE,"E2.0");var subQ2=makeQuery(id+"F0.imprint","INTERSECT",VERTEX,{"disambiguationData":[OD(0.0)],"derivedFrom":[subQ1,subQ0]});Q23=makeQuery(id+"F0.imprint","IMPRINT",FACE,{"disambiguationData":[TD([[makeQuery(id+"F0.imprint","IMPRINT",EDGE,{"disambiguationData":[TD([[subQ2,-1.0]])],"derivedFrom":subQ1}),1.0]])]});}
            var Q24;
            {var subQ0=sQuery(id+"F0.wireOp",EDGE,"E6.13.0");var subQ1=sQuery(id+"F0.wireOp",EDGE,"E2.0");var subQ2=makeQuery(id+"F0.imprint","INTERSECT",VERTEX,{"disambiguationData":[OD(0.0)],"derivedFrom":[subQ1,subQ0]});Q24=makeQuery(id+"F0.imprint","IMPRINT",FACE,{"disambiguationData":[TD([[makeQuery(id+"F0.imprint","IMPRINT",EDGE,{"disambiguationData":[TD([[subQ2,-1.0]])],"derivedFrom":subQ1}),1.0]])]});}
            var Q25;
            {var subQ0=sQuery(id+"F0.wireOp",EDGE,"E4.5.0");var subQ1=sQuery(id+"F0.wireOp",EDGE,"E2.0");var subQ2=makeQuery(id+"F0.imprint","INTERSECT",VERTEX,{"disambiguationData":[OD(0.0)],"derivedFrom":[subQ1,subQ0]});Q25=makeQuery(id+"F0.imprint","IMPRINT",FACE,{"disambiguationData":[TD([[makeQuery(id+"F0.imprint","IMPRINT",EDGE,{"disambiguationData":[TD([[subQ2,-1.0]])],"derivedFrom":subQ1}),1.0]])]});}
            var Q26;
            {var subQ0=sQuery(id+"F0.wireOp",EDGE,"E6.13.0");var subQ1=sQuery(id+"F0.wireOp",EDGE,"E2.0");var subQ2=makeQuery(id+"F0.imprint","INTERSECT",VERTEX,{"disambiguationData":[OD(0.0)],"derivedFrom":[subQ1,subQ0]});Q26=makeQuery(id+"F0.imprint","IMPRINT",FACE,{"disambiguationData":[TD([[makeQuery(id+"F0.imprint","IMPRINT",EDGE,{"disambiguationData":[TD([[subQ2,-1.0]])],"derivedFrom":subQ1}),-1.0]])]});}
            var Q27;
            {var subQ0=sQuery(id+"F0.wireOp",EDGE,"E4.5.0");var subQ1=sQuery(id+"F0.wireOp",EDGE,"E2.0");var subQ2=makeQuery(id+"F0.imprint","INTERSECT",VERTEX,{"disambiguationData":[OD(0.0)],"derivedFrom":[subQ1,subQ0]});Q27=makeQuery(id+"F0.imprint","IMPRINT",FACE,{"disambiguationData":[TD([[makeQuery(id+"F0.imprint","IMPRINT",EDGE,{"disambiguationData":[TD([[subQ2,-1.0]])],"derivedFrom":subQ1}),-1.0]])]});}
            var Q28;
            {var subQ0=sQuery(id+"F0.wireOp",EDGE,"E4.4.0");var subQ1=sQuery(id+"F0.wireOp",EDGE,"E2.0");var subQ2=makeQuery(id+"F0.imprint","INTERSECT",VERTEX,{"disambiguationData":[OD(0.0)],"derivedFrom":[subQ1,subQ0]});Q28=makeQuery(id+"F0.imprint","IMPRINT",FACE,{"disambiguationData":[TD([[makeQuery(id+"F0.imprint","IMPRINT",EDGE,{"disambiguationData":[TD([[subQ2,-1.0]])],"derivedFrom":subQ1}),-1.0]])]});}
            var Q29;
            {var subQ0=sQuery(id+"F0.wireOp",EDGE,"E6.12.0");var subQ1=sQuery(id+"F0.wireOp",EDGE,"E2.0");var subQ2=makeQuery(id+"F0.imprint","INTERSECT",VERTEX,{"disambiguationData":[OD(0.0)],"derivedFrom":[subQ1,subQ0]});Q29=makeQuery(id+"F0.imprint","IMPRINT",FACE,{"disambiguationData":[TD([[makeQuery(id+"F0.imprint","IMPRINT",EDGE,{"disambiguationData":[TD([[subQ2,-1.0]])],"derivedFrom":subQ1}),-1.0]])]});}
            var Q30;
            {var subQ0=sQuery(id+"F0.wireOp",EDGE,"E6.12.0");var subQ1=sQuery(id+"F0.wireOp",EDGE,"E2.0");var subQ2=makeQuery(id+"F0.imprint","INTERSECT",VERTEX,{"disambiguationData":[OD(0.0)],"derivedFrom":[subQ1,subQ0]});Q30=makeQuery(id+"F0.imprint","IMPRINT",FACE,{"disambiguationData":[TD([[makeQuery(id+"F0.imprint","IMPRINT",EDGE,{"disambiguationData":[TD([[subQ2,-1.0]])],"derivedFrom":subQ1}),1.0]])]});}
            var Q31;
            {var subQ0=sQuery(id+"F0.wireOp",EDGE,"E4.4.0");var subQ1=sQuery(id+"F0.wireOp",EDGE,"E2.0");var subQ2=makeQuery(id+"F0.imprint","INTERSECT",VERTEX,{"disambiguationData":[OD(0.0)],"derivedFrom":[subQ1,subQ0]});Q31=makeQuery(id+"F0.imprint","IMPRINT",FACE,{"disambiguationData":[TD([[makeQuery(id+"F0.imprint","IMPRINT",EDGE,{"disambiguationData":[TD([[subQ2,-1.0]])],"derivedFrom":subQ1}),1.0]])]});}
            var Q32;
            {var subQ0=sQuery(id+"F0.wireOp",EDGE,"E4.3.0");var subQ1=sQuery(id+"F0.wireOp",EDGE,"E2.0");var subQ2=makeQuery(id+"F0.imprint","INTERSECT",VERTEX,{"disambiguationData":[OD(0.0)],"derivedFrom":[subQ1,subQ0]});Q32=makeQuery(id+"F0.imprint","IMPRINT",FACE,{"disambiguationData":[TD([[makeQuery(id+"F0.imprint","IMPRINT",EDGE,{"disambiguationData":[TD([[subQ2,-1.0]])],"derivedFrom":subQ1}),1.0]])]});}
            var Q33;
            {var subQ0=sQuery(id+"F0.wireOp",EDGE,"E6.11.0");var subQ1=sQuery(id+"F0.wireOp",EDGE,"E2.0");var subQ2=makeQuery(id+"F0.imprint","INTERSECT",VERTEX,{"disambiguationData":[OD(0.0)],"derivedFrom":[subQ1,subQ0]});Q33=makeQuery(id+"F0.imprint","IMPRINT",FACE,{"disambiguationData":[TD([[makeQuery(id+"F0.imprint","IMPRINT",EDGE,{"disambiguationData":[TD([[subQ2,-1.0]])],"derivedFrom":subQ1}),1.0]])]});}
            var Q34;
            {var subQ0=sQuery(id+"F0.wireOp",EDGE,"E6.11.0");var subQ1=sQuery(id+"F0.wireOp",EDGE,"E2.0");var subQ2=makeQuery(id+"F0.imprint","INTERSECT",VERTEX,{"disambiguationData":[OD(0.0)],"derivedFrom":[subQ1,subQ0]});Q34=makeQuery(id+"F0.imprint","IMPRINT",FACE,{"disambiguationData":[TD([[makeQuery(id+"F0.imprint","IMPRINT",EDGE,{"disambiguationData":[TD([[subQ2,-1.0]])],"derivedFrom":subQ1}),-1.0]])]});}
            var Q35;
            {var subQ0=sQuery(id+"F0.wireOp",EDGE,"E4.3.0");var subQ1=sQuery(id+"F0.wireOp",EDGE,"E2.0");var subQ2=makeQuery(id+"F0.imprint","INTERSECT",VERTEX,{"disambiguationData":[OD(0.0)],"derivedFrom":[subQ1,subQ0]});Q35=makeQuery(id+"F0.imprint","IMPRINT",FACE,{"disambiguationData":[TD([[makeQuery(id+"F0.imprint","IMPRINT",EDGE,{"disambiguationData":[TD([[subQ2,-1.0]])],"derivedFrom":subQ1}),-1.0]])]});}
            var Q36;
            {var subQ0=sQuery(id+"F0.wireOp",EDGE,"E6.10.0");var subQ1=sQuery(id+"F0.wireOp",EDGE,"E2.0");var subQ2=makeQuery(id+"F0.imprint","INTERSECT",VERTEX,{"disambiguationData":[OD(0.0)],"derivedFrom":[subQ1,subQ0]});Q36=makeQuery(id+"F0.imprint","IMPRINT",FACE,{"disambiguationData":[TD([[makeQuery(id+"F0.imprint","IMPRINT",EDGE,{"disambiguationData":[TD([[subQ2,-1.0]])],"derivedFrom":subQ1}),-1.0]])]});}
            var Q37;
            {var subQ0=sQuery(id+"F0.wireOp",EDGE,"E6.10.0");var subQ1=sQuery(id+"F0.wireOp",EDGE,"E2.0");var subQ2=makeQuery(id+"F0.imprint","INTERSECT",VERTEX,{"disambiguationData":[OD(0.0)],"derivedFrom":[subQ1,subQ0]});Q37=makeQuery(id+"F0.imprint","IMPRINT",FACE,{"disambiguationData":[TD([[makeQuery(id+"F0.imprint","IMPRINT",EDGE,{"disambiguationData":[TD([[subQ2,-1.0]])],"derivedFrom":subQ1}),1.0]])]});}
            var Q38;
            {var subQ0=sQuery(id+"F0.wireOp",EDGE,"E4.2.0");var subQ1=sQuery(id+"F0.wireOp",EDGE,"E2.0");var subQ2=makeQuery(id+"F0.imprint","INTERSECT",VERTEX,{"disambiguationData":[OD(0.0)],"derivedFrom":[subQ1,subQ0]});Q38=makeQuery(id+"F0.imprint","IMPRINT",FACE,{"disambiguationData":[TD([[makeQuery(id+"F0.imprint","IMPRINT",EDGE,{"disambiguationData":[TD([[subQ2,-1.0]])],"derivedFrom":subQ1}),1.0]])]});}
            var Q39;
            {var subQ0=sQuery(id+"F0.wireOp",EDGE,"E4.2.0");var subQ1=sQuery(id+"F0.wireOp",EDGE,"E2.0");var subQ2=makeQuery(id+"F0.imprint","INTERSECT",VERTEX,{"disambiguationData":[OD(0.0)],"derivedFrom":[subQ1,subQ0]});Q39=makeQuery(id+"F0.imprint","IMPRINT",FACE,{"disambiguationData":[TD([[makeQuery(id+"F0.imprint","IMPRINT",EDGE,{"disambiguationData":[TD([[subQ2,-1.0]])],"derivedFrom":subQ1}),-1.0]])]});}
            var Q40;
            {var subQ0=sQuery(id+"F0.wireOp",EDGE,"E6.9.0");var subQ1=sQuery(id+"F0.wireOp",EDGE,"E2.0");var subQ2=makeQuery(id+"F0.imprint","INTERSECT",VERTEX,{"disambiguationData":[OD(0.0)],"derivedFrom":[subQ1,subQ0]});Q40=makeQuery(id+"F0.imprint","IMPRINT",FACE,{"disambiguationData":[TD([[makeQuery(id+"F0.imprint","IMPRINT",EDGE,{"disambiguationData":[TD([[subQ2,-1.0]])],"derivedFrom":subQ1}),1.0]])]});}
            var Q41;
            {var subQ0=sQuery(id+"F0.wireOp",EDGE,"E6.9.0");var subQ1=sQuery(id+"F0.wireOp",EDGE,"E2.0");var subQ2=makeQuery(id+"F0.imprint","INTERSECT",VERTEX,{"disambiguationData":[OD(0.0)],"derivedFrom":[subQ1,subQ0]});Q41=makeQuery(id+"F0.imprint","IMPRINT",FACE,{"disambiguationData":[TD([[makeQuery(id+"F0.imprint","IMPRINT",EDGE,{"disambiguationData":[TD([[subQ2,-1.0]])],"derivedFrom":subQ1}),-1.0]])]});}
            var Q42;
            {var subQ0=sQuery(id+"F0.wireOp",EDGE,"E4.1.0");var subQ1=sQuery(id+"F0.wireOp",EDGE,"E2.0");var subQ2=makeQuery(id+"F0.imprint","INTERSECT",VERTEX,{"disambiguationData":[OD(0.0)],"derivedFrom":[subQ1,subQ0]});Q42=makeQuery(id+"F0.imprint","IMPRINT",FACE,{"disambiguationData":[TD([[makeQuery(id+"F0.imprint","IMPRINT",EDGE,{"disambiguationData":[TD([[subQ2,-1.0]])],"derivedFrom":subQ1}),1.0]])]});}
            var Q43;
            {var subQ0=sQuery(id+"F0.wireOp",EDGE,"E4.1.0");var subQ1=sQuery(id+"F0.wireOp",EDGE,"E2.0");var subQ2=makeQuery(id+"F0.imprint","INTERSECT",VERTEX,{"disambiguationData":[OD(0.0)],"derivedFrom":[subQ1,subQ0]});Q43=makeQuery(id+"F0.imprint","IMPRINT",FACE,{"disambiguationData":[TD([[makeQuery(id+"F0.imprint","IMPRINT",EDGE,{"disambiguationData":[TD([[subQ2,-1.0]])],"derivedFrom":subQ1}),-1.0]])]});}
            var Q44;
            {var subQ0=sQuery(id+"F0.wireOp",EDGE,"E3");var subQ1=sQuery(id+"F0.wireOp",EDGE,"E2.0");var subQ2=makeQuery(id+"F0.imprint","INTERSECT",VERTEX,{"disambiguationData":[OD(0.0)],"derivedFrom":[subQ1,subQ0]});Q44=makeQuery(id+"F0.imprint","IMPRINT",FACE,{"disambiguationData":[TD([[makeQuery(id+"F0.imprint","IMPRINT",EDGE,{"disambiguationData":[TD([[subQ2,-1.0]])],"derivedFrom":subQ1}),-1.0]])]});}
            var Q45;
            {var subQ0=sQuery(id+"F0.wireOp",EDGE,"E6.8.0");var subQ1=sQuery(id+"F0.wireOp",EDGE,"E2.0");var subQ2=makeQuery(id+"F0.imprint","INTERSECT",VERTEX,{"disambiguationData":[OD(0.0)],"derivedFrom":[subQ1,subQ0]});Q45=makeQuery(id+"F0.imprint","IMPRINT",FACE,{"disambiguationData":[TD([[makeQuery(id+"F0.imprint","IMPRINT",EDGE,{"disambiguationData":[TD([[subQ2,-1.0]])],"derivedFrom":subQ1}),-1.0]])]});}
            var Q46;
            {var subQ0=sQuery(id+"F0.wireOp",EDGE,"E6.8.0");var subQ1=sQuery(id+"F0.wireOp",EDGE,"E2.0");var subQ2=makeQuery(id+"F0.imprint","INTERSECT",VERTEX,{"disambiguationData":[OD(0.0)],"derivedFrom":[subQ1,subQ0]});Q46=makeQuery(id+"F0.imprint","IMPRINT",FACE,{"disambiguationData":[TD([[makeQuery(id+"F0.imprint","IMPRINT",EDGE,{"disambiguationData":[TD([[subQ2,-1.0]])],"derivedFrom":subQ1}),1.0]])]});}
            var Q47;
            {var subQ0=sQuery(id+"F0.wireOp",EDGE,"E3");var subQ1=sQuery(id+"F0.wireOp",EDGE,"E2.0");var subQ2=makeQuery(id+"F0.imprint","INTERSECT",VERTEX,{"disambiguationData":[OD(0.0)],"derivedFrom":[subQ1,subQ0]});Q47=makeQuery(id+"F0.imprint","IMPRINT",FACE,{"disambiguationData":[TD([[makeQuery(id+"F0.imprint","IMPRINT",EDGE,{"disambiguationData":[TD([[subQ2,-1.0]])],"derivedFrom":subQ1}),1.0]])]});}
            var Q48;
            {var subQ0=sQuery(id+"F0.wireOp",EDGE,"E4.15.0");var subQ1=sQuery(id+"F0.wireOp",EDGE,"E2.0");var subQ2=makeQuery(id+"F0.imprint","INTERSECT",VERTEX,{"disambiguationData":[OD(0.0)],"derivedFrom":[subQ1,subQ0]});Q48=makeQuery(id+"F0.imprint","IMPRINT",FACE,{"disambiguationData":[TD([[makeQuery(id+"F0.imprint","IMPRINT",EDGE,{"disambiguationData":[TD([[subQ2,-1.0]])],"derivedFrom":subQ1}),1.0]])]});}
            var Q49;
            {var subQ0=sQuery(id+"F0.wireOp",EDGE,"E6.7.0");var subQ1=sQuery(id+"F0.wireOp",EDGE,"E2.0");var subQ2=makeQuery(id+"F0.imprint","INTERSECT",VERTEX,{"disambiguationData":[OD(0.0)],"derivedFrom":[subQ1,subQ0]});Q49=makeQuery(id+"F0.imprint","IMPRINT",FACE,{"disambiguationData":[TD([[makeQuery(id+"F0.imprint","IMPRINT",EDGE,{"disambiguationData":[TD([[subQ2,-1.0]])],"derivedFrom":subQ1}),1.0]])]});}
            var Q50;
            {var subQ0=sQuery(id+"F0.wireOp",EDGE,"E6.7.0");var subQ1=sQuery(id+"F0.wireOp",EDGE,"E2.0");var subQ2=makeQuery(id+"F0.imprint","INTERSECT",VERTEX,{"disambiguationData":[OD(0.0)],"derivedFrom":[subQ1,subQ0]});Q50=makeQuery(id+"F0.imprint","IMPRINT",FACE,{"disambiguationData":[TD([[makeQuery(id+"F0.imprint","IMPRINT",EDGE,{"disambiguationData":[TD([[subQ2,-1.0]])],"derivedFrom":subQ1}),-1.0]])]});}
            var Q51;
            {var subQ0=sQuery(id+"F0.wireOp",EDGE,"E4.15.0");var subQ1=sQuery(id+"F0.wireOp",EDGE,"E2.0");var subQ2=makeQuery(id+"F0.imprint","INTERSECT",VERTEX,{"disambiguationData":[OD(0.0)],"derivedFrom":[subQ1,subQ0]});Q51=makeQuery(id+"F0.imprint","IMPRINT",FACE,{"disambiguationData":[TD([[makeQuery(id+"F0.imprint","IMPRINT",EDGE,{"disambiguationData":[TD([[subQ2,-1.0]])],"derivedFrom":subQ1}),-1.0]])]});}
            var Q52;
            {var subQ0=sQuery(id+"F0.wireOp",EDGE,"E4.14.0");var subQ1=sQuery(id+"F0.wireOp",EDGE,"E2.0");var subQ2=makeQuery(id+"F0.imprint","INTERSECT",VERTEX,{"disambiguationData":[OD(0.0)],"derivedFrom":[subQ1,subQ0]});Q52=makeQuery(id+"F0.imprint","IMPRINT",FACE,{"disambiguationData":[TD([[makeQuery(id+"F0.imprint","IMPRINT",EDGE,{"disambiguationData":[TD([[subQ2,-1.0]])],"derivedFrom":subQ1}),1.0]])]});}
            var Q53;
            {var subQ0=sQuery(id+"F0.wireOp",EDGE,"E6.6.0");var subQ1=sQuery(id+"F0.wireOp",EDGE,"E2.0");var subQ2=makeQuery(id+"F0.imprint","INTERSECT",VERTEX,{"disambiguationData":[OD(0.0)],"derivedFrom":[subQ1,subQ0]});Q53=makeQuery(id+"F0.imprint","IMPRINT",FACE,{"disambiguationData":[TD([[makeQuery(id+"F0.imprint","IMPRINT",EDGE,{"disambiguationData":[TD([[subQ2,-1.0]])],"derivedFrom":subQ1}),1.0]])]});}
            var Q54;
            {var subQ0=sQuery(id+"F0.wireOp",EDGE,"E6.6.0");var subQ1=sQuery(id+"F0.wireOp",EDGE,"E2.0");var subQ2=makeQuery(id+"F0.imprint","INTERSECT",VERTEX,{"disambiguationData":[OD(0.0)],"derivedFrom":[subQ1,subQ0]});Q54=makeQuery(id+"F0.imprint","IMPRINT",FACE,{"disambiguationData":[TD([[makeQuery(id+"F0.imprint","IMPRINT",EDGE,{"disambiguationData":[TD([[subQ2,-1.0]])],"derivedFrom":subQ1}),-1.0]])]});}
            var Q55;
            {var subQ0=sQuery(id+"F0.wireOp",EDGE,"E4.14.0");var subQ1=sQuery(id+"F0.wireOp",EDGE,"E2.0");var subQ2=makeQuery(id+"F0.imprint","INTERSECT",VERTEX,{"disambiguationData":[OD(0.0)],"derivedFrom":[subQ1,subQ0]});Q55=makeQuery(id+"F0.imprint","IMPRINT",FACE,{"disambiguationData":[TD([[makeQuery(id+"F0.imprint","IMPRINT",EDGE,{"disambiguationData":[TD([[subQ2,-1.0]])],"derivedFrom":subQ1}),-1.0]])]});}
            var Q56;
            {var subQ0=sQuery(id+"F0.wireOp",EDGE,"E4.13.0");var subQ1=sQuery(id+"F0.wireOp",EDGE,"E2.0");var subQ2=makeQuery(id+"F0.imprint","INTERSECT",VERTEX,{"disambiguationData":[OD(0.0)],"derivedFrom":[subQ1,subQ0]});Q56=makeQuery(id+"F0.imprint","IMPRINT",FACE,{"disambiguationData":[TD([[makeQuery(id+"F0.imprint","IMPRINT",EDGE,{"disambiguationData":[TD([[subQ2,-1.0]])],"derivedFrom":subQ1}),-1.0]])]});}
            var Q57;
            {var subQ0=sQuery(id+"F0.wireOp",EDGE,"E6.5.0");var subQ1=sQuery(id+"F0.wireOp",EDGE,"E2.0");var subQ2=makeQuery(id+"F0.imprint","INTERSECT",VERTEX,{"disambiguationData":[OD(0.0)],"derivedFrom":[subQ1,subQ0]});Q57=makeQuery(id+"F0.imprint","IMPRINT",FACE,{"disambiguationData":[TD([[makeQuery(id+"F0.imprint","IMPRINT",EDGE,{"disambiguationData":[TD([[subQ2,-1.0]])],"derivedFrom":subQ1}),-1.0]])]});}
            var Q58;
            {var subQ0=sQuery(id+"F0.wireOp",EDGE,"E6.5.0");var subQ1=sQuery(id+"F0.wireOp",EDGE,"E2.0");var subQ2=makeQuery(id+"F0.imprint","INTERSECT",VERTEX,{"disambiguationData":[OD(0.0)],"derivedFrom":[subQ1,subQ0]});Q58=makeQuery(id+"F0.imprint","IMPRINT",FACE,{"disambiguationData":[TD([[makeQuery(id+"F0.imprint","IMPRINT",EDGE,{"disambiguationData":[TD([[subQ2,-1.0]])],"derivedFrom":subQ1}),1.0]])]});}
            var Q59;
            {var subQ0=sQuery(id+"F0.wireOp",EDGE,"E4.13.0");var subQ1=sQuery(id+"F0.wireOp",EDGE,"E2.0");var subQ2=makeQuery(id+"F0.imprint","INTERSECT",VERTEX,{"disambiguationData":[OD(0.0)],"derivedFrom":[subQ1,subQ0]});Q59=makeQuery(id+"F0.imprint","IMPRINT",FACE,{"disambiguationData":[TD([[makeQuery(id+"F0.imprint","IMPRINT",EDGE,{"disambiguationData":[TD([[subQ2,-1.0]])],"derivedFrom":subQ1}),1.0]])]});}
            var Q60;
            {var subQ0=sQuery(id+"F0.wireOp",EDGE,"E4.12.0");var subQ1=sQuery(id+"F0.wireOp",EDGE,"E2.0");var subQ2=makeQuery(id+"F0.imprint","INTERSECT",VERTEX,{"disambiguationData":[OD(0.0)],"derivedFrom":[subQ1,subQ0]});Q60=makeQuery(id+"F0.imprint","IMPRINT",FACE,{"disambiguationData":[TD([[makeQuery(id+"F0.imprint","IMPRINT",EDGE,{"disambiguationData":[TD([[subQ2,1.0]])],"derivedFrom":subQ1}),1.0]])]});}
            var Q61;
            {var subQ0=sQuery(id+"F0.wireOp",EDGE,"E6.4.0");var subQ1=sQuery(id+"F0.wireOp",EDGE,"E2.0");var subQ2=makeQuery(id+"F0.imprint","INTERSECT",VERTEX,{"disambiguationData":[OD(0.0)],"derivedFrom":[subQ1,subQ0]});Q61=makeQuery(id+"F0.imprint","IMPRINT",FACE,{"disambiguationData":[TD([[makeQuery(id+"F0.imprint","IMPRINT",EDGE,{"disambiguationData":[TD([[subQ2,1.0]])],"derivedFrom":subQ1}),1.0]])]});}
            var Q62;
            {var subQ0=sQuery(id+"F0.wireOp",EDGE,"E6.4.0");var subQ1=sQuery(id+"F0.wireOp",EDGE,"E2.0");var subQ2=makeQuery(id+"F0.imprint","INTERSECT",VERTEX,{"disambiguationData":[OD(0.0)],"derivedFrom":[subQ1,subQ0]});Q62=makeQuery(id+"F0.imprint","IMPRINT",FACE,{"disambiguationData":[TD([[makeQuery(id+"F0.imprint","IMPRINT",EDGE,{"disambiguationData":[TD([[subQ2,1.0]])],"derivedFrom":subQ1}),-1.0]])]});}
            var Q63;
            {var subQ0=sQuery(id+"F0.wireOp",EDGE,"E4.12.0");var subQ1=sQuery(id+"F0.wireOp",EDGE,"E2.0");var subQ2=makeQuery(id+"F0.imprint","INTERSECT",VERTEX,{"disambiguationData":[OD(0.0)],"derivedFrom":[subQ1,subQ0]});Q63=makeQuery(id+"F0.imprint","IMPRINT",FACE,{"disambiguationData":[TD([[makeQuery(id+"F0.imprint","IMPRINT",EDGE,{"disambiguationData":[TD([[subQ2,1.0]])],"derivedFrom":subQ1}),-1.0]])]});}
            extrude(context, id + "F4", {"entities" : qUnion([Q0, Q1, Q2, Q3, Q4, Q5, Q6, Q7, Q8, Q9, Q10, Q11, Q12, Q13, Q14, Q15, Q16, Q17, Q18, Q19, Q20, Q21, Q22, Q23, Q24, Q25, Q26, Q27, Q28, Q29, Q30, Q31, Q32, Q33, Q34, Q35, Q36, Q37, Q38, Q39, Q40, Q41, Q42, Q43, Q44, Q45, Q46, Q47, Q48, Q49, Q50, Q51, Q52, Q53, Q54, Q55, Q56, Q57, Q58, Q59, Q60, Q61, Q62, Q63]), "oppositeDirection" : true, "depth" : 5 * mm, "hasSecondDirection" : true, "secondDirectionOppositeDirection" : true, "secondDirectionDepth" : .1 * mm});
        }
        {
            var Q0;
            Q0=makeQuery(id+"F1.opExtrude","CAP_EDGE",EDGE,{"disambiguationData":[OSD([sQuery(id+"F0.wireOp",EDGE,"E4.2.0")])],"isStart":false});
            var Q1;
            Q1=makeQuery(id+"F1.opExtrude","CAP_EDGE",EDGE,{"disambiguationData":[OSD([sQuery(id+"F0.wireOp",EDGE,"E4.1.0")])],"isStart":false});
            var Q2;
            Q2=makeQuery(id+"F1.opExtrude","CAP_EDGE",EDGE,{"disambiguationData":[OSD([sQuery(id+"F0.wireOp",EDGE,"E3")])],"isStart":false});
            var Q3;
            Q3=makeQuery(id+"F1.opExtrude","CAP_EDGE",EDGE,{"disambiguationData":[OSD([sQuery(id+"F0.wireOp",EDGE,"E4.15.0")])],"isStart":false});
            var Q4;
            Q4=makeQuery(id+"F1.opExtrude","CAP_EDGE",EDGE,{"disambiguationData":[OSD([sQuery(id+"F0.wireOp",EDGE,"E4.14.0")])],"isStart":false});
            var Q5;
            Q5=makeQuery(id+"F1.opExtrude","CAP_EDGE",EDGE,{"disambiguationData":[OSD([sQuery(id+"F0.wireOp",EDGE,"E4.13.0")])],"isStart":false});
            var Q6;
            Q6=makeQuery(id+"F1.opExtrude","CAP_EDGE",EDGE,{"disambiguationData":[OSD([sQuery(id+"F0.wireOp",EDGE,"E4.12.0")])],"isStart":false});
            var Q7;
            Q7=makeQuery(id+"F1.opExtrude","CAP_EDGE",EDGE,{"disambiguationData":[OSD([sQuery(id+"F0.wireOp",EDGE,"E4.11.0")])],"isStart":false});
            var Q8;
            Q8=makeQuery(id+"F1.opExtrude","CAP_EDGE",EDGE,{"disambiguationData":[OSD([sQuery(id+"F0.wireOp",EDGE,"E4.10.0")])],"isStart":false});
            var Q9;
            Q9=makeQuery(id+"F1.opExtrude","CAP_EDGE",EDGE,{"disambiguationData":[OSD([sQuery(id+"F0.wireOp",EDGE,"E4.9.0")])],"isStart":false});
            var Q10;
            Q10=makeQuery(id+"F1.opExtrude","CAP_EDGE",EDGE,{"disambiguationData":[OSD([sQuery(id+"F0.wireOp",EDGE,"E4.8.0")])],"isStart":false});
            var Q11;
            Q11=makeQuery(id+"F1.opExtrude","CAP_EDGE",EDGE,{"disambiguationData":[OSD([sQuery(id+"F0.wireOp",EDGE,"E4.7.0")])],"isStart":false});
            var Q12;
            Q12=makeQuery(id+"F1.opExtrude","CAP_EDGE",EDGE,{"disambiguationData":[OSD([sQuery(id+"F0.wireOp",EDGE,"E4.6.0")])],"isStart":false});
            var Q13;
            Q13=makeQuery(id+"F1.opExtrude","CAP_EDGE",EDGE,{"disambiguationData":[OSD([sQuery(id+"F0.wireOp",EDGE,"E4.5.0")])],"isStart":false});
            var Q14;
            Q14=makeQuery(id+"F1.opExtrude","CAP_EDGE",EDGE,{"disambiguationData":[OSD([sQuery(id+"F0.wireOp",EDGE,"E4.4.0")])],"isStart":false});
            var Q15;
            Q15=makeQuery(id+"F1.opExtrude","CAP_EDGE",EDGE,{"disambiguationData":[OSD([sQuery(id+"F0.wireOp",EDGE,"E4.3.0")])],"isStart":false});
            var Q16;
            Q16=makeQuery(id+"F4.opExtrude","CAP_EDGE",EDGE,{"disambiguationData":[OSD([sQuery(id+"F0.wireOp",EDGE,"E4.15.0")])],"isStart":false});
            var Q17;
            Q17=makeQuery(id+"F4.opExtrude","CAP_EDGE",EDGE,{"disambiguationData":[OSD([sQuery(id+"F0.wireOp",EDGE,"E3")])],"isStart":false});
            var Q18;
            Q18=makeQuery(id+"F4.opExtrude","CAP_EDGE",EDGE,{"disambiguationData":[OSD([sQuery(id+"F0.wireOp",EDGE,"E4.1.0")])],"isStart":false});
            var Q19;
            Q19=makeQuery(id+"F4.opExtrude","CAP_EDGE",EDGE,{"disambiguationData":[OSD([sQuery(id+"F0.wireOp",EDGE,"E4.2.0")])],"isStart":false});
            var Q20;
            Q20=makeQuery(id+"F4.opExtrude","CAP_EDGE",EDGE,{"disambiguationData":[OSD([sQuery(id+"F0.wireOp",EDGE,"E4.3.0")])],"isStart":false});
            var Q21;
            Q21=makeQuery(id+"F4.opExtrude","CAP_EDGE",EDGE,{"disambiguationData":[OSD([sQuery(id+"F0.wireOp",EDGE,"E4.4.0")])],"isStart":false});
            var Q22;
            Q22=makeQuery(id+"F4.opExtrude","CAP_EDGE",EDGE,{"disambiguationData":[OSD([sQuery(id+"F0.wireOp",EDGE,"E4.5.0")])],"isStart":false});
            var Q23;
            Q23=makeQuery(id+"F4.opExtrude","CAP_EDGE",EDGE,{"disambiguationData":[OSD([sQuery(id+"F0.wireOp",EDGE,"E4.6.0")])],"isStart":false});
            var Q24;
            Q24=makeQuery(id+"F4.opExtrude","CAP_EDGE",EDGE,{"disambiguationData":[OSD([sQuery(id+"F0.wireOp",EDGE,"E4.7.0")])],"isStart":false});
            var Q25;
            Q25=makeQuery(id+"F4.opExtrude","CAP_EDGE",EDGE,{"disambiguationData":[OSD([sQuery(id+"F0.wireOp",EDGE,"E4.8.0")])],"isStart":false});
            var Q26;
            Q26=makeQuery(id+"F4.opExtrude","CAP_EDGE",EDGE,{"disambiguationData":[OSD([sQuery(id+"F0.wireOp",EDGE,"E4.9.0")])],"isStart":false});
            var Q27;
            Q27=makeQuery(id+"F4.opExtrude","CAP_EDGE",EDGE,{"disambiguationData":[OSD([sQuery(id+"F0.wireOp",EDGE,"E4.10.0")])],"isStart":false});
            var Q28;
            Q28=makeQuery(id+"F4.opExtrude","CAP_EDGE",EDGE,{"disambiguationData":[OSD([sQuery(id+"F0.wireOp",EDGE,"E4.11.0")])],"isStart":false});
            var Q29;
            Q29=makeQuery(id+"F4.opExtrude","CAP_EDGE",EDGE,{"disambiguationData":[OSD([sQuery(id+"F0.wireOp",EDGE,"E4.12.0")])],"isStart":false});
            var Q30;
            Q30=makeQuery(id+"F4.opExtrude","CAP_EDGE",EDGE,{"disambiguationData":[OSD([sQuery(id+"F0.wireOp",EDGE,"E4.13.0")])],"isStart":false});
            var Q31;
            Q31=makeQuery(id+"F4.opExtrude","CAP_EDGE",EDGE,{"disambiguationData":[OSD([sQuery(id+"F0.wireOp",EDGE,"E4.14.0")])],"isStart":false});
            fillet(context, id + "F5", {"entities" : qUnion([Q0, Q1, Q2, Q3, Q4, Q5, Q6, Q7, Q8, Q9, Q10, Q11, Q12, Q13, Q14, Q15, Q16, Q17, Q18, Q19, Q20, Q21, Q22, Q23, Q24, Q25, Q26, Q27, Q28, Q29, Q30, Q31]), "radius" : 2 * mm, "tangentPropagation" : true, "allowEdgeOverflow" : false});
        }
        {
            var Q0;
            {var subQ0=sQuery(id+"F0.wireOp",EDGE,"E6.3.0");var subQ1=sQuery(id+"F0.wireOp",EDGE,"E2.0");var subQ2=makeQuery(id+"F0.imprint","INTERSECT",VERTEX,{"disambiguationData":[OD(0.0)],"derivedFrom":[subQ1,subQ0]});Q0=makeQuery(id+"F0.imprint","IMPRINT",FACE,{"disambiguationData":[TD([[makeQuery(id+"F0.imprint","IMPRINT",EDGE,{"disambiguationData":[TD([[subQ2,-1.0]])],"derivedFrom":subQ1}),-1.0]])]});}
            var Q1;
            {var subQ0=sQuery(id+"F0.wireOp",EDGE,"E6.3.0");var subQ1=sQuery(id+"F0.wireOp",EDGE,"E2.0");var subQ2=makeQuery(id+"F0.imprint","INTERSECT",VERTEX,{"disambiguationData":[OD(0.0)],"derivedFrom":[subQ1,subQ0]});Q1=makeQuery(id+"F0.imprint","IMPRINT",FACE,{"disambiguationData":[TD([[makeQuery(id+"F0.imprint","IMPRINT",EDGE,{"disambiguationData":[TD([[subQ2,-1.0]])],"derivedFrom":subQ1}),1.0]])]});}
            var Q2;
            {var subQ0=sQuery(id+"F0.wireOp",EDGE,"E6.4.0");var subQ1=sQuery(id+"F0.wireOp",EDGE,"E2.0");var subQ2=makeQuery(id+"F0.imprint","INTERSECT",VERTEX,{"disambiguationData":[OD(0.0)],"derivedFrom":[subQ1,subQ0]});Q2=makeQuery(id+"F0.imprint","IMPRINT",FACE,{"disambiguationData":[TD([[makeQuery(id+"F0.imprint","IMPRINT",EDGE,{"disambiguationData":[TD([[subQ2,1.0]])],"derivedFrom":subQ1}),1.0]])]});}
            var Q3;
            {var subQ0=sQuery(id+"F0.wireOp",EDGE,"E6.4.0");var subQ1=sQuery(id+"F0.wireOp",EDGE,"E2.0");var subQ2=makeQuery(id+"F0.imprint","INTERSECT",VERTEX,{"disambiguationData":[OD(0.0)],"derivedFrom":[subQ1,subQ0]});Q3=makeQuery(id+"F0.imprint","IMPRINT",FACE,{"disambiguationData":[TD([[makeQuery(id+"F0.imprint","IMPRINT",EDGE,{"disambiguationData":[TD([[subQ2,1.0]])],"derivedFrom":subQ1}),-1.0]])]});}
            var Q4;
            {var subQ0=sQuery(id+"F0.wireOp",EDGE,"E6.5.0");var subQ1=sQuery(id+"F0.wireOp",EDGE,"E2.0");var subQ2=makeQuery(id+"F0.imprint","INTERSECT",VERTEX,{"disambiguationData":[OD(0.0)],"derivedFrom":[subQ1,subQ0]});Q4=makeQuery(id+"F0.imprint","IMPRINT",FACE,{"disambiguationData":[TD([[makeQuery(id+"F0.imprint","IMPRINT",EDGE,{"disambiguationData":[TD([[subQ2,-1.0]])],"derivedFrom":subQ1}),-1.0]])]});}
            var Q5;
            {var subQ0=sQuery(id+"F0.wireOp",EDGE,"E6.5.0");var subQ1=sQuery(id+"F0.wireOp",EDGE,"E2.0");var subQ2=makeQuery(id+"F0.imprint","INTERSECT",VERTEX,{"disambiguationData":[OD(0.0)],"derivedFrom":[subQ1,subQ0]});Q5=makeQuery(id+"F0.imprint","IMPRINT",FACE,{"disambiguationData":[TD([[makeQuery(id+"F0.imprint","IMPRINT",EDGE,{"disambiguationData":[TD([[subQ2,-1.0]])],"derivedFrom":subQ1}),1.0]])]});}
            var Q6;
            {var subQ0=sQuery(id+"F0.wireOp",EDGE,"E6.6.0");var subQ1=sQuery(id+"F0.wireOp",EDGE,"E2.0");var subQ2=makeQuery(id+"F0.imprint","INTERSECT",VERTEX,{"disambiguationData":[OD(0.0)],"derivedFrom":[subQ1,subQ0]});Q6=makeQuery(id+"F0.imprint","IMPRINT",FACE,{"disambiguationData":[TD([[makeQuery(id+"F0.imprint","IMPRINT",EDGE,{"disambiguationData":[TD([[subQ2,-1.0]])],"derivedFrom":subQ1}),-1.0]])]});}
            var Q7;
            {var subQ0=sQuery(id+"F0.wireOp",EDGE,"E6.6.0");var subQ1=sQuery(id+"F0.wireOp",EDGE,"E2.0");var subQ2=makeQuery(id+"F0.imprint","INTERSECT",VERTEX,{"disambiguationData":[OD(0.0)],"derivedFrom":[subQ1,subQ0]});Q7=makeQuery(id+"F0.imprint","IMPRINT",FACE,{"disambiguationData":[TD([[makeQuery(id+"F0.imprint","IMPRINT",EDGE,{"disambiguationData":[TD([[subQ2,-1.0]])],"derivedFrom":subQ1}),1.0]])]});}
            var Q8;
            {var subQ0=sQuery(id+"F0.wireOp",EDGE,"E6.7.0");var subQ1=sQuery(id+"F0.wireOp",EDGE,"E2.0");var subQ2=makeQuery(id+"F0.imprint","INTERSECT",VERTEX,{"disambiguationData":[OD(0.0)],"derivedFrom":[subQ1,subQ0]});Q8=makeQuery(id+"F0.imprint","IMPRINT",FACE,{"disambiguationData":[TD([[makeQuery(id+"F0.imprint","IMPRINT",EDGE,{"disambiguationData":[TD([[subQ2,-1.0]])],"derivedFrom":subQ1}),-1.0]])]});}
            var Q9;
            {var subQ0=sQuery(id+"F0.wireOp",EDGE,"E6.7.0");var subQ1=sQuery(id+"F0.wireOp",EDGE,"E2.0");var subQ2=makeQuery(id+"F0.imprint","INTERSECT",VERTEX,{"disambiguationData":[OD(0.0)],"derivedFrom":[subQ1,subQ0]});Q9=makeQuery(id+"F0.imprint","IMPRINT",FACE,{"disambiguationData":[TD([[makeQuery(id+"F0.imprint","IMPRINT",EDGE,{"disambiguationData":[TD([[subQ2,-1.0]])],"derivedFrom":subQ1}),1.0]])]});}
            var Q10;
            {var subQ0=sQuery(id+"F0.wireOp",EDGE,"E6.8.0");var subQ1=sQuery(id+"F0.wireOp",EDGE,"E2.0");var subQ2=makeQuery(id+"F0.imprint","INTERSECT",VERTEX,{"disambiguationData":[OD(0.0)],"derivedFrom":[subQ1,subQ0]});Q10=makeQuery(id+"F0.imprint","IMPRINT",FACE,{"disambiguationData":[TD([[makeQuery(id+"F0.imprint","IMPRINT",EDGE,{"disambiguationData":[TD([[subQ2,-1.0]])],"derivedFrom":subQ1}),-1.0]])]});}
            var Q11;
            {var subQ0=sQuery(id+"F0.wireOp",EDGE,"E6.8.0");var subQ1=sQuery(id+"F0.wireOp",EDGE,"E2.0");var subQ2=makeQuery(id+"F0.imprint","INTERSECT",VERTEX,{"disambiguationData":[OD(0.0)],"derivedFrom":[subQ1,subQ0]});Q11=makeQuery(id+"F0.imprint","IMPRINT",FACE,{"disambiguationData":[TD([[makeQuery(id+"F0.imprint","IMPRINT",EDGE,{"disambiguationData":[TD([[subQ2,-1.0]])],"derivedFrom":subQ1}),1.0]])]});}
            var Q12;
            {var subQ0=sQuery(id+"F0.wireOp",EDGE,"E6.9.0");var subQ1=sQuery(id+"F0.wireOp",EDGE,"E2.0");var subQ2=makeQuery(id+"F0.imprint","INTERSECT",VERTEX,{"disambiguationData":[OD(0.0)],"derivedFrom":[subQ1,subQ0]});Q12=makeQuery(id+"F0.imprint","IMPRINT",FACE,{"disambiguationData":[TD([[makeQuery(id+"F0.imprint","IMPRINT",EDGE,{"disambiguationData":[TD([[subQ2,-1.0]])],"derivedFrom":subQ1}),-1.0]])]});}
            var Q13;
            {var subQ0=sQuery(id+"F0.wireOp",EDGE,"E6.9.0");var subQ1=sQuery(id+"F0.wireOp",EDGE,"E2.0");var subQ2=makeQuery(id+"F0.imprint","INTERSECT",VERTEX,{"disambiguationData":[OD(0.0)],"derivedFrom":[subQ1,subQ0]});Q13=makeQuery(id+"F0.imprint","IMPRINT",FACE,{"disambiguationData":[TD([[makeQuery(id+"F0.imprint","IMPRINT",EDGE,{"disambiguationData":[TD([[subQ2,-1.0]])],"derivedFrom":subQ1}),1.0]])]});}
            var Q14;
            {var subQ0=sQuery(id+"F0.wireOp",EDGE,"E6.10.0");var subQ1=sQuery(id+"F0.wireOp",EDGE,"E2.0");var subQ2=makeQuery(id+"F0.imprint","INTERSECT",VERTEX,{"disambiguationData":[OD(0.0)],"derivedFrom":[subQ1,subQ0]});Q14=makeQuery(id+"F0.imprint","IMPRINT",FACE,{"disambiguationData":[TD([[makeQuery(id+"F0.imprint","IMPRINT",EDGE,{"disambiguationData":[TD([[subQ2,-1.0]])],"derivedFrom":subQ1}),1.0]])]});}
            var Q15;
            {var subQ0=sQuery(id+"F0.wireOp",EDGE,"E6.10.0");var subQ1=sQuery(id+"F0.wireOp",EDGE,"E2.0");var subQ2=makeQuery(id+"F0.imprint","INTERSECT",VERTEX,{"disambiguationData":[OD(0.0)],"derivedFrom":[subQ1,subQ0]});Q15=makeQuery(id+"F0.imprint","IMPRINT",FACE,{"disambiguationData":[TD([[makeQuery(id+"F0.imprint","IMPRINT",EDGE,{"disambiguationData":[TD([[subQ2,-1.0]])],"derivedFrom":subQ1}),-1.0]])]});}
            var Q16;
            {var subQ0=sQuery(id+"F0.wireOp",EDGE,"E6.11.0");var subQ1=sQuery(id+"F0.wireOp",EDGE,"E2.0");var subQ2=makeQuery(id+"F0.imprint","INTERSECT",VERTEX,{"disambiguationData":[OD(0.0)],"derivedFrom":[subQ1,subQ0]});Q16=makeQuery(id+"F0.imprint","IMPRINT",FACE,{"disambiguationData":[TD([[makeQuery(id+"F0.imprint","IMPRINT",EDGE,{"disambiguationData":[TD([[subQ2,-1.0]])],"derivedFrom":subQ1}),1.0]])]});}
            var Q17;
            {var subQ0=sQuery(id+"F0.wireOp",EDGE,"E6.11.0");var subQ1=sQuery(id+"F0.wireOp",EDGE,"E2.0");var subQ2=makeQuery(id+"F0.imprint","INTERSECT",VERTEX,{"disambiguationData":[OD(0.0)],"derivedFrom":[subQ1,subQ0]});Q17=makeQuery(id+"F0.imprint","IMPRINT",FACE,{"disambiguationData":[TD([[makeQuery(id+"F0.imprint","IMPRINT",EDGE,{"disambiguationData":[TD([[subQ2,-1.0]])],"derivedFrom":subQ1}),-1.0]])]});}
            var Q18;
            {var subQ0=sQuery(id+"F0.wireOp",EDGE,"E6.12.0");var subQ1=sQuery(id+"F0.wireOp",EDGE,"E2.0");var subQ2=makeQuery(id+"F0.imprint","INTERSECT",VERTEX,{"disambiguationData":[OD(0.0)],"derivedFrom":[subQ1,subQ0]});Q18=makeQuery(id+"F0.imprint","IMPRINT",FACE,{"disambiguationData":[TD([[makeQuery(id+"F0.imprint","IMPRINT",EDGE,{"disambiguationData":[TD([[subQ2,-1.0]])],"derivedFrom":subQ1}),-1.0]])]});}
            var Q19;
            {var subQ0=sQuery(id+"F0.wireOp",EDGE,"E6.12.0");var subQ1=sQuery(id+"F0.wireOp",EDGE,"E2.0");var subQ2=makeQuery(id+"F0.imprint","INTERSECT",VERTEX,{"disambiguationData":[OD(0.0)],"derivedFrom":[subQ1,subQ0]});Q19=makeQuery(id+"F0.imprint","IMPRINT",FACE,{"disambiguationData":[TD([[makeQuery(id+"F0.imprint","IMPRINT",EDGE,{"disambiguationData":[TD([[subQ2,-1.0]])],"derivedFrom":subQ1}),1.0]])]});}
            var Q20;
            {var subQ0=sQuery(id+"F0.wireOp",EDGE,"E6.13.0");var subQ1=sQuery(id+"F0.wireOp",EDGE,"E2.0");var subQ2=makeQuery(id+"F0.imprint","INTERSECT",VERTEX,{"disambiguationData":[OD(0.0)],"derivedFrom":[subQ1,subQ0]});Q20=makeQuery(id+"F0.imprint","IMPRINT",FACE,{"disambiguationData":[TD([[makeQuery(id+"F0.imprint","IMPRINT",EDGE,{"disambiguationData":[TD([[subQ2,-1.0]])],"derivedFrom":subQ1}),1.0]])]});}
            var Q21;
            {var subQ0=sQuery(id+"F0.wireOp",EDGE,"E6.13.0");var subQ1=sQuery(id+"F0.wireOp",EDGE,"E2.0");var subQ2=makeQuery(id+"F0.imprint","INTERSECT",VERTEX,{"disambiguationData":[OD(0.0)],"derivedFrom":[subQ1,subQ0]});Q21=makeQuery(id+"F0.imprint","IMPRINT",FACE,{"disambiguationData":[TD([[makeQuery(id+"F0.imprint","IMPRINT",EDGE,{"disambiguationData":[TD([[subQ2,-1.0]])],"derivedFrom":subQ1}),-1.0]])]});}
            var Q22;
            {var subQ0=sQuery(id+"F0.wireOp",EDGE,"E6.14.0");var subQ1=sQuery(id+"F0.wireOp",EDGE,"E2.0");var subQ2=makeQuery(id+"F0.imprint","INTERSECT",VERTEX,{"disambiguationData":[OD(0.0)],"derivedFrom":[subQ1,subQ0]});Q22=makeQuery(id+"F0.imprint","IMPRINT",FACE,{"disambiguationData":[TD([[makeQuery(id+"F0.imprint","IMPRINT",EDGE,{"disambiguationData":[TD([[subQ2,-1.0]])],"derivedFrom":subQ1}),1.0]])]});}
            var Q23;
            {var subQ0=sQuery(id+"F0.wireOp",EDGE,"E6.14.0");var subQ1=sQuery(id+"F0.wireOp",EDGE,"E2.0");var subQ2=makeQuery(id+"F0.imprint","INTERSECT",VERTEX,{"disambiguationData":[OD(0.0)],"derivedFrom":[subQ1,subQ0]});Q23=makeQuery(id+"F0.imprint","IMPRINT",FACE,{"disambiguationData":[TD([[makeQuery(id+"F0.imprint","IMPRINT",EDGE,{"disambiguationData":[TD([[subQ2,-1.0]])],"derivedFrom":subQ1}),-1.0]])]});}
            var Q24;
            {var subQ0=sQuery(id+"F0.wireOp",EDGE,"E6.15.0");var subQ1=sQuery(id+"F0.wireOp",EDGE,"E2.0");var subQ2=makeQuery(id+"F0.imprint","INTERSECT",VERTEX,{"disambiguationData":[OD(0.0)],"derivedFrom":[subQ1,subQ0]});Q24=makeQuery(id+"F0.imprint","IMPRINT",FACE,{"disambiguationData":[TD([[makeQuery(id+"F0.imprint","IMPRINT",EDGE,{"disambiguationData":[TD([[subQ2,-1.0]])],"derivedFrom":subQ1}),1.0]])]});}
            var Q25;
            {var subQ0=sQuery(id+"F0.wireOp",EDGE,"E6.15.0");var subQ1=sQuery(id+"F0.wireOp",EDGE,"E2.0");var subQ2=makeQuery(id+"F0.imprint","INTERSECT",VERTEX,{"disambiguationData":[OD(0.0)],"derivedFrom":[subQ1,subQ0]});Q25=makeQuery(id+"F0.imprint","IMPRINT",FACE,{"disambiguationData":[TD([[makeQuery(id+"F0.imprint","IMPRINT",EDGE,{"disambiguationData":[TD([[subQ2,-1.0]])],"derivedFrom":subQ1}),-1.0]])]});}
            var Q26;
            {var subQ0=sQuery(id+"F0.wireOp",EDGE,"E5.0");var subQ1=sQuery(id+"F0.wireOp",EDGE,"E2.0");var subQ2=makeQuery(id+"F0.imprint","INTERSECT",VERTEX,{"disambiguationData":[OD(0.0)],"derivedFrom":[subQ1,subQ0]});Q26=makeQuery(id+"F0.imprint","IMPRINT",FACE,{"disambiguationData":[TD([[makeQuery(id+"F0.imprint","IMPRINT",EDGE,{"disambiguationData":[TD([[subQ2,-1.0]])],"derivedFrom":subQ1}),1.0]])]});}
            var Q27;
            {var subQ0=sQuery(id+"F0.wireOp",EDGE,"E5.0");var subQ1=sQuery(id+"F0.wireOp",EDGE,"E2.0");var subQ2=makeQuery(id+"F0.imprint","INTERSECT",VERTEX,{"disambiguationData":[OD(0.0)],"derivedFrom":[subQ1,subQ0]});Q27=makeQuery(id+"F0.imprint","IMPRINT",FACE,{"disambiguationData":[TD([[makeQuery(id+"F0.imprint","IMPRINT",EDGE,{"disambiguationData":[TD([[subQ2,-1.0]])],"derivedFrom":subQ1}),-1.0]])]});}
            var Q28;
            {var subQ0=sQuery(id+"F0.wireOp",EDGE,"E6.1.0");var subQ1=sQuery(id+"F0.wireOp",EDGE,"E2.0");var subQ2=makeQuery(id+"F0.imprint","INTERSECT",VERTEX,{"disambiguationData":[OD(0.0)],"derivedFrom":[subQ1,subQ0]});Q28=makeQuery(id+"F0.imprint","IMPRINT",FACE,{"disambiguationData":[TD([[makeQuery(id+"F0.imprint","IMPRINT",EDGE,{"disambiguationData":[TD([[subQ2,-1.0]])],"derivedFrom":subQ1}),1.0]])]});}
            var Q29;
            {var subQ0=sQuery(id+"F0.wireOp",EDGE,"E6.1.0");var subQ1=sQuery(id+"F0.wireOp",EDGE,"E2.0");var subQ2=makeQuery(id+"F0.imprint","INTERSECT",VERTEX,{"disambiguationData":[OD(0.0)],"derivedFrom":[subQ1,subQ0]});Q29=makeQuery(id+"F0.imprint","IMPRINT",FACE,{"disambiguationData":[TD([[makeQuery(id+"F0.imprint","IMPRINT",EDGE,{"disambiguationData":[TD([[subQ2,-1.0]])],"derivedFrom":subQ1}),-1.0]])]});}
            var Q30;
            {var subQ0=sQuery(id+"F0.wireOp",EDGE,"E6.2.0");var subQ1=sQuery(id+"F0.wireOp",EDGE,"E2.0");var subQ2=makeQuery(id+"F0.imprint","INTERSECT",VERTEX,{"disambiguationData":[OD(0.0)],"derivedFrom":[subQ1,subQ0]});Q30=makeQuery(id+"F0.imprint","IMPRINT",FACE,{"disambiguationData":[TD([[makeQuery(id+"F0.imprint","IMPRINT",EDGE,{"disambiguationData":[TD([[subQ2,-1.0]])],"derivedFrom":subQ1}),1.0]])]});}
            var Q31;
            {var subQ0=sQuery(id+"F0.wireOp",EDGE,"E6.2.0");var subQ1=sQuery(id+"F0.wireOp",EDGE,"E2.0");var subQ2=makeQuery(id+"F0.imprint","INTERSECT",VERTEX,{"disambiguationData":[OD(0.0)],"derivedFrom":[subQ1,subQ0]});Q31=makeQuery(id+"F0.imprint","IMPRINT",FACE,{"disambiguationData":[TD([[makeQuery(id+"F0.imprint","IMPRINT",EDGE,{"disambiguationData":[TD([[subQ2,-1.0]])],"derivedFrom":subQ1}),-1.0]])]});}
            extrude(context, id + "F6", {"entities" : qUnion([Q0, Q1, Q2, Q3, Q4, Q5, Q6, Q7, Q8, Q9, Q10, Q11, Q12, Q13, Q14, Q15, Q16, Q17, Q18, Q19, Q20, Q21, Q22, Q23, Q24, Q25, Q26, Q27, Q28, Q29, Q30, Q31]), "depth" : .4 * mm, "hasSecondDirection" : true, "secondDirectionOppositeDirection" : true, "secondDirectionDepth" : .4 * mm});
        }
    });
